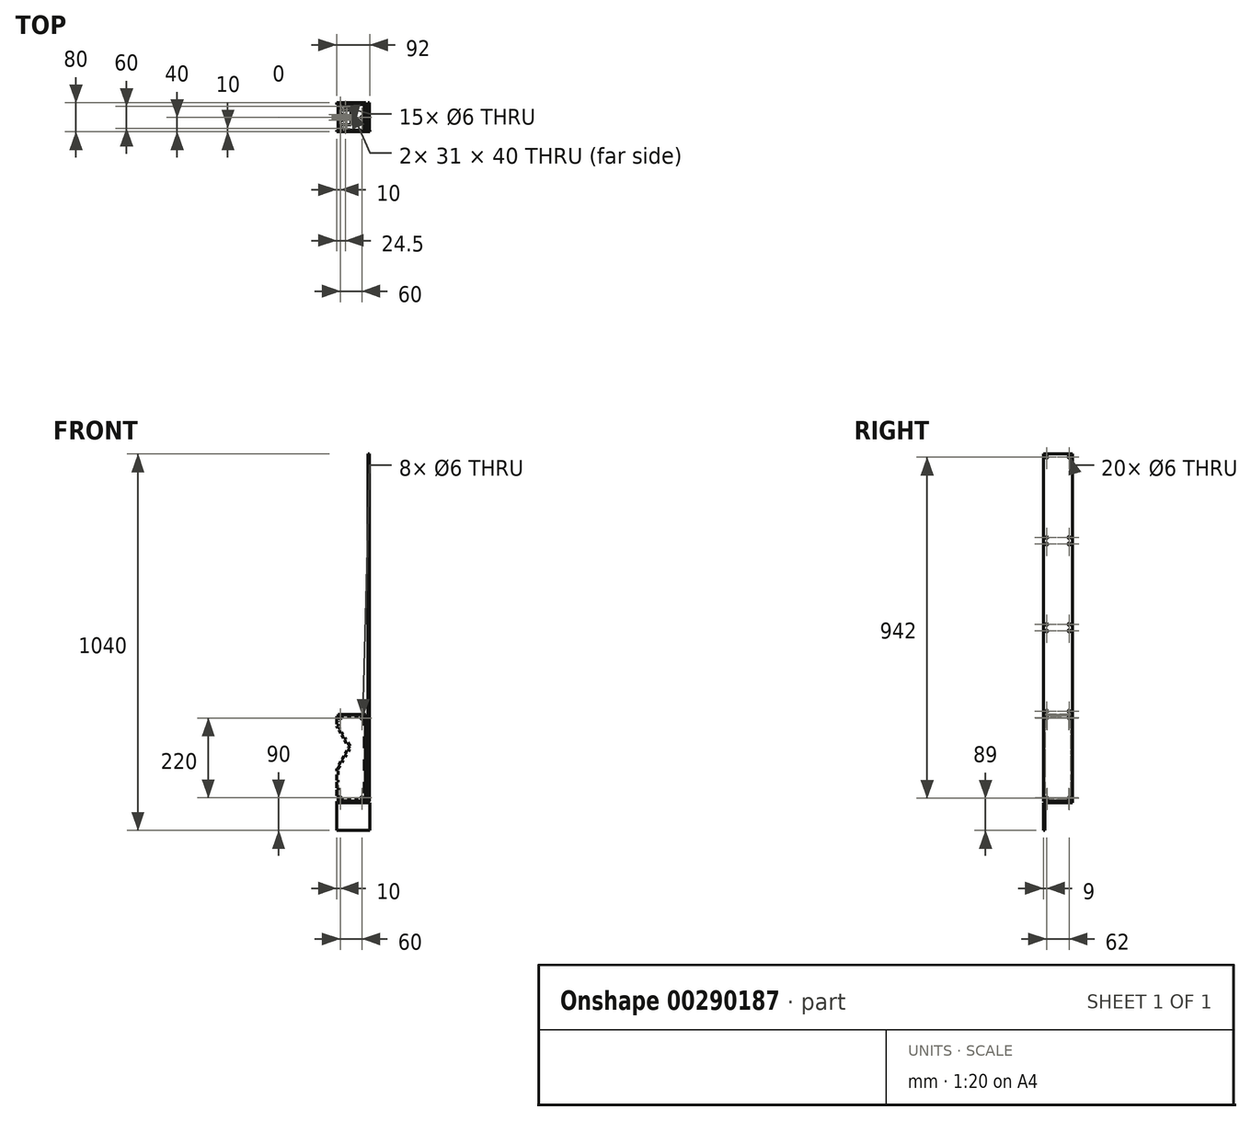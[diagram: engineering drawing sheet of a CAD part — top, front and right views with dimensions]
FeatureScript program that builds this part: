
annotation { "Feature Type Name" : "Feature", "Feature Type Description" : "" }
export const myFeature = defineFeature(function(context is Context, id is Id, definition is map)
    precondition{}
    {
        {
            assignVariable(context, id + "F0", {"name" : "WT", "anyValue" : 4});
        }
        {
            assignVariable(context, id + "F1", {"name" : "HD", "anyValue" : 3});
        }
        {
            var Q0;
            Q0=qCreatedBy(makeId("Front.planeOp"),FACE);
            var sketch = newSketch(context, id + "F2", { "sketchPlane" : qUnion([Q0])});
            skLineSegment(sketch, "E0", {"start": v(0, 0) * mm, "end": v(0, 240) * mm});
            skLineSegment(sketch, "E1", {"start": v(0, 120) * mm, "end": v(-80, 120) * mm, "construction": true});
            skLineSegment(sketch, "E2", {"start": v(0, 0) * mm, "end": v(-80, 0) * mm});
            skLineSegment(sketch, "E3", {"start": v(-80, 0) * mm, "end": v(-80, 90.56) * mm});
            skLineSegment(sketch, "E4", {"start": v(-80, 90.56) * mm, "end": v(-46, 149.44) * mm});
            skLineSegment(sketch, "E5", {"start": v(-46, 149.44) * mm, "end": v(-80, 208.33) * mm});
            skLineSegment(sketch, "E6", {"start": v(-80, 208.33) * mm, "end": v(-80, 240) * mm});
            skLineSegment(sketch, "E7", {"start": v(-80, 240) * mm, "end": v(0, 240) * mm});
            skLineSegment(sketch, "E8", {"start": v(-80, 90.56) * mm, "end": v(0, 90.56) * mm, "construction": true});
            skLineSegment(sketch, "E9", {"start": v(-80, 208.33) * mm, "end": v(0, 208.33) * mm, "construction": true});
            skPoint(sketch, "E10", {"position": v(-63, 120) * mm});
            skLineSegment(sketch, "E11", {"start": v(-80, 90.56) * mm, "end": v(-76, 90.56) * mm});
            skLineSegment(sketch, "E12", {"start": v(-76, 90.56) * mm, "end": v(-76, 0) * mm});
            skLineSegment(sketch, "E13", {"start": v(-4, 0) * mm, "end": v(-4, 240) * mm});
            skLineSegment(sketch, "E14", {"start": v(0, 236) * mm, "end": v(-80, 236) * mm});
            skLineSegment(sketch, "E15", {"start": v(-76, 240) * mm, "end": v(-76, 208.33) * mm});
            skLineSegment(sketch, "E16", {"start": v(-80, 208.33) * mm, "end": v(-76, 208.33) * mm});
            skLineSegment(sketch, "E17", {"start": v(-80, 4) * mm, "end": v(0, 4) * mm});
            skLineSegment(sketch, "E18", {"start": v(-80, 90.56) * mm, "end": v(-76.54, 88.56) * mm});
            skLineSegment(sketch, "E19", {"start": v(-76.54, 88.56) * mm, "end": v(-42.54, 147.44) * mm});
            skLineSegment(sketch, "E20", {"start": v(-80, 208.33) * mm, "end": v(-76.54, 210.33) * mm});
            skLineSegment(sketch, "E21", {"start": v(-76.54, 210.33) * mm, "end": v(-41.38, 149.44) * mm});
            skLineSegment(sketch, "E22", {"start": v(-46, 149.44) * mm, "end": v(-44.85, 147.44) * mm});
            skLineSegment(sketch, "E23", {"start": v(-44.85, 147.44) * mm, "end": v(-41.38, 149.44) * mm});
            skLineSegment(sketch, "E24", {"start": v(-42.54, 147.44) * mm, "end": v(-41.38, 149.44) * mm});
            skLineSegment(sketch, "E25", {"start": v(-46, 149.44) * mm, "end": v(-44.85, 151.44) * mm});
            skLineSegment(sketch, "E26", {"start": v(-44.85, 151.44) * mm, "end": v(-41.38, 149.44) * mm});
            skLineSegment(sketch, "E27", {"start": v(-75.54, 208.6) * mm, "end": v(-79, 206.6) * mm});
            skLineSegment(sketch, "E28", {"start": v(-46.58, 150.44) * mm, "end": v(-43.11, 152.44) * mm});
            skPoint(sketch, "E29", {"position": v(-79, 206.6) * mm});
            skPoint(sketch, "E30", {"position": v(-46.58, 150.44) * mm});
            skPoint(sketch, "E31", {"position": v(-80, 88.56) * mm});
            skCircle(sketch, "E32", {"center": v(-70, 230) * mm, "radius": 3 * mm});
            skLineSegment(sketch, "E33", {"start": v(-40, 208.33) * mm, "end": v(-40, 225.54) * mm, "construction": true});
            skCircle(sketch, "E34.MirrorC", {"center": v(-10, 230) * mm, "radius": 3 * mm});
            skCircle(sketch, "E35.MirrorC", {"center": v(-70, 10) * mm, "radius": 3 * mm});
            skCircle(sketch, "E36.MirrorC", {"center": v(-10, 10) * mm, "radius": 3 * mm});
            skSolve(sketch);
        }
        {
            var Q0;
            Q0=qCreatedBy(makeId("Front.planeOp"),FACE);
            var sketch = newSketch(context, id + "F3", { "sketchPlane" : qUnion([Q0])});
            skLineSegment(sketch, "E37.0", {"start": v(-80, 240) * mm, "end": v(0, 240) * mm});
            skLineSegment(sketch, "E37.1", {"start": v(-80, 208.33) * mm, "end": v(-80, 240) * mm});
            skLineSegment(sketch, "E37.2", {"start": v(-46, 149.44) * mm, "end": v(-80, 208.33) * mm});
            skLineSegment(sketch, "E37.3", {"start": v(-80, 90.56) * mm, "end": v(-46, 149.44) * mm});
            skLineSegment(sketch, "E37.4", {"start": v(-80, 0) * mm, "end": v(-80, 90.56) * mm});
            skLineSegment(sketch, "E37.5", {"start": v(0, 0) * mm, "end": v(-80, 0) * mm});
            skLineSegment(sketch, "E37.6", {"start": v(0, 0) * mm, "end": v(0, 240) * mm});
            skCircle(sketch, "E38.0", {"center": v(-70, 230) * mm, "radius": 3 * mm});
            skCircle(sketch, "E38.1", {"center": v(-10, 230) * mm, "radius": 3 * mm});
            skCircle(sketch, "E38.2", {"center": v(-70, 10) * mm, "radius": 3 * mm});
            skCircle(sketch, "E38.3", {"center": v(-10, 10) * mm, "radius": 3 * mm});
            skLineSegment(sketch, "E39", {"start": v(0, -80) * mm, "end": v(-80, -80) * mm});
            skLineSegment(sketch, "E40", {"start": v(-80, -80) * mm, "end": v(-80, 0) * mm});
            skLineSegment(sketch, "E41", {"start": v(0, 0) * mm, "end": v(12, 0) * mm});
            skLineSegment(sketch, "E42", {"start": v(12, 0) * mm, "end": v(12, -80) * mm});
            skLineSegment(sketch, "E43", {"start": v(12, -80) * mm, "end": v(0, -80) * mm});
            skSolve(sketch);
        }
        {
            var Q0;
            Q0=sQuery(id+"F2.wireOp",EDGE,"E7");
            cPlane(context, id + "F4", {"entities" : qUnion([Q0]), "cplaneType" : CPlaneType.LINE_ANGLE, "offset" : 25 * mm, "angle" : 90 * degree, "width" : 150 * mm, "height" : 150 * mm});
        }
        {
            var Q0;
            Q0=qCreatedBy(id+"F4.planeOp",FACE);
            var sketch = newSketch(context, id + "F5", { "sketchPlane" : qUnion([Q0])});
            skLineSegment(sketch, "E44.0", {"start": v(-80, 0) * mm, "end": v(0, 0) * mm});
            skLineSegment(sketch, "E45", {"start": v(-80, 0) * mm, "end": v(-80, 80) * mm});
            skLineSegment(sketch, "E46", {"start": v(-80, 80) * mm, "end": v(0, 80) * mm});
            skLineSegment(sketch, "E47", {"start": v(0, 80) * mm, "end": v(0, 0) * mm});
            skLineSegment(sketch, "E48", {"start": v(0, 40) * mm, "end": v(-80, 40) * mm, "construction": true});
            skLineSegment(sketch, "E49", {"start": v(-80, 76) * mm, "end": v(0, 76) * mm});
            skLineSegment(sketch, "E50", {"start": v(-70, 80) * mm, "end": v(-70, 76) * mm});
            skLineSegment(sketch, "E51.1.0.0", {"start": v(-60, 80) * mm, "end": v(-60, 76) * mm});
            skLineSegment(sketch, "E51.2.0.0", {"start": v(-50, 80) * mm, "end": v(-50, 76) * mm});
            skLineSegment(sketch, "E51.3.0.0", {"start": v(-40, 80) * mm, "end": v(-40, 76) * mm});
            skLineSegment(sketch, "E51.4.0.0", {"start": v(-30, 80) * mm, "end": v(-30, 76) * mm});
            skLineSegment(sketch, "E51.5.0.0", {"start": v(-20, 80) * mm, "end": v(-20, 76) * mm});
            skLineSegment(sketch, "E51.6.0.0", {"start": v(-10, 80) * mm, "end": v(-10, 76) * mm});
            skLineSegment(sketch, "E51.direction1", {"start": v(-70, 76) * mm, "end": v(-60, 76) * mm, "construction": true});
            skLineSegment(sketch, "E52.MirrorCS", {"start": v(-80, 4) * mm, "end": v(0, 4) * mm});
            skLineSegment(sketch, "E53.MirrorCS", {"start": v(-70, 0) * mm, "end": v(-70, 4) * mm});
            skLineSegment(sketch, "E54.MirrorCS", {"start": v(-60, 0) * mm, "end": v(-60, 4) * mm});
            skLineSegment(sketch, "E55.MirrorCS", {"start": v(-50, 0) * mm, "end": v(-50, 4) * mm});
            skLineSegment(sketch, "E56.MirrorCS", {"start": v(-40, 0) * mm, "end": v(-40, 4) * mm});
            skLineSegment(sketch, "E57.MirrorCS", {"start": v(-30, 0) * mm, "end": v(-30, 4) * mm});
            skLineSegment(sketch, "E58.MirrorCS", {"start": v(-20, 0) * mm, "end": v(-20, 4) * mm});
            skLineSegment(sketch, "E59.MirrorCS", {"start": v(-10, 0) * mm, "end": v(-10, 4) * mm});
            skLineSegment(sketch, "E60", {"start": v(-76, 80) * mm, "end": v(-76, 0) * mm});
            skLineSegment(sketch, "E61", {"start": v(-80, 71.1) * mm, "end": v(-76, 71.1) * mm});
            skLineSegment(sketch, "E62.0.1.0", {"start": v(-80, 62.34) * mm, "end": v(-76, 62.34) * mm});
            skLineSegment(sketch, "E62.0.2.0", {"start": v(-80, 53.6) * mm, "end": v(-76, 53.6) * mm});
            skLineSegment(sketch, "E62.0.3.0", {"start": v(-80, 44.84) * mm, "end": v(-76, 44.84) * mm});
            skLineSegment(sketch, "E62.0.4.0", {"start": v(-80, 36.1) * mm, "end": v(-76, 36.1) * mm});
            skLineSegment(sketch, "E62.0.5.0", {"start": v(-80, 27.34) * mm, "end": v(-76, 27.34) * mm});
            skLineSegment(sketch, "E62.0.6.0", {"start": v(-80, 18.6) * mm, "end": v(-76, 18.6) * mm});
            skLineSegment(sketch, "E62.direction1", {"start": v(-86.03, 71.1) * mm, "end": v(-80, 71.1) * mm, "construction": true});
            skLineSegment(sketch, "E62.direction2", {"start": v(-80, 71.1) * mm, "end": v(-80, 62.34) * mm, "construction": true});
            skLineSegment(sketch, "E63", {"start": v(-40, 40) * mm, "end": v(-40, 50.28) * mm, "construction": true});
            skLineSegment(sketch, "E64.MirrorCS", {"start": v(0, 18.6) * mm, "end": v(-4, 18.6) * mm});
            skLineSegment(sketch, "E65.MirrorCS", {"start": v(0, 27.34) * mm, "end": v(-4, 27.34) * mm});
            skLineSegment(sketch, "E66.MirrorCS", {"start": v(0, 36.1) * mm, "end": v(-4, 36.1) * mm});
            skLineSegment(sketch, "E67.MirrorCS", {"start": v(0, 44.84) * mm, "end": v(-4, 44.84) * mm});
            skLineSegment(sketch, "E68.MirrorCS", {"start": v(0, 53.6) * mm, "end": v(-4, 53.6) * mm});
            skLineSegment(sketch, "E69.MirrorCS", {"start": v(0, 62.34) * mm, "end": v(-4, 62.34) * mm});
            skLineSegment(sketch, "E70.MirrorCS", {"start": v(0, 71.1) * mm, "end": v(-4, 71.1) * mm});
            skLineSegment(sketch, "E71.MirrorCS", {"start": v(-4, 80) * mm, "end": v(-4, 0) * mm});
            skLineSegment(sketch, "E72.bottom", {"start": v(-40, 20) * mm, "end": v(-71, 20) * mm});
            skLineSegment(sketch, "E72.top", {"start": v(-40, 60) * mm, "end": v(-71, 60) * mm});
            skLineSegment(sketch, "E72.left", {"start": v(-9, 40) * mm, "end": v(-9, 60) * mm, "construction": true});
            skLineSegment(sketch, "E72.right", {"start": v(-71, 20) * mm, "end": v(-71, 60) * mm});
            skPoint(sketch, "E72.middle", {"position": v(-40, 40) * mm});
            skCircle(sketch, "E73", {"center": v(-10, 40) * mm, "radius": 3 * mm});
            skCircle(sketch, "E74.MirrorC", {"center": v(-70, 70) * mm, "radius": 3 * mm});
            skLineSegment(sketch, "E75", {"start": v(-40, 20) * mm, "end": v(-40, 60) * mm});
            skPoint(sketch, "E76.orphan", {"position": v(-9, 20) * mm});
            skCircle(sketch, "E77.MirrorC", {"center": v(-70, 10) * mm, "radius": 3 * mm});
            skLineSegment(sketch, "E78.0.0.7", {"start": v(-80, 9.84) * mm, "end": v(-76, 9.84) * mm});
            skLineSegment(sketch, "E79.MirrorCS", {"start": v(0, 9.84) * mm, "end": v(-4, 9.84) * mm});
            skSolve(sketch);
        }
        {
            var Q0;
            Q0=sQuery(id+"F2.wireOp",EDGE,"E0");
            cPlane(context, id + "F6", {"entities" : qUnion([Q0]), "cplaneType" : CPlaneType.LINE_ANGLE, "offset" : 25 * mm, "angle" : 0 * degree, "width" : 150 * mm, "height" : 150 * mm});
        }
        {
            var Q0;
            Q0=qCreatedBy(id+"F6.planeOp",FACE);
            var sketch = newSketch(context, id + "F7", { "sketchPlane" : qUnion([Q0])});
            skLineSegment(sketch, "E80.0", {"start": v(0, 0) * mm, "end": v(0, 240) * mm});
            skLineSegment(sketch, "E81.0", {"start": v(80, 240) * mm, "end": v(0, 240) * mm});
            skLineSegment(sketch, "E82", {"start": v(80, 240) * mm, "end": v(80, 0) * mm});
            skLineSegment(sketch, "E83", {"start": v(80, 0) * mm, "end": v(0, 0) * mm});
            skLineSegment(sketch, "E84", {"start": v(4, 240) * mm, "end": v(4, 0) * mm});
            skLineSegment(sketch, "E85", {"start": v(0, 210) * mm, "end": v(4, 210) * mm});
            skLineSegment(sketch, "E86.0.1.0", {"start": v(0, 178.75) * mm, "end": v(4, 178.75) * mm});
            skLineSegment(sketch, "E86.0.2.0", {"start": v(0, 147.5) * mm, "end": v(4, 147.5) * mm});
            skLineSegment(sketch, "E86.0.3.0", {"start": v(0, 116.25) * mm, "end": v(4, 116.25) * mm});
            skLineSegment(sketch, "E86.0.4.0", {"start": v(0, 85) * mm, "end": v(4, 85) * mm});
            skLineSegment(sketch, "E86.0.5.0", {"start": v(0, 53.75) * mm, "end": v(4, 53.75) * mm});
            skLineSegment(sketch, "E86.0.6.0", {"start": v(0, 22.5) * mm, "end": v(4, 22.5) * mm});
            skLineSegment(sketch, "E86.direction1", {"start": v(-5.68, 210) * mm, "end": v(0, 210) * mm, "construction": true});
            skLineSegment(sketch, "E86.direction2", {"start": v(0, 210) * mm, "end": v(0, 178.75) * mm, "construction": true});
            skLineSegment(sketch, "E87", {"start": v(40, 240) * mm, "end": v(40, 220.49) * mm, "construction": true});
            skPoint(sketch, "E87.endSnap0", {"position": v(40, 240) * mm});
            skLineSegment(sketch, "E88.MirrorCS", {"start": v(76, 240) * mm, "end": v(76, 0) * mm});
            skLineSegment(sketch, "E89.MirrorCS", {"start": v(80, 210) * mm, "end": v(76, 210) * mm});
            skLineSegment(sketch, "E90.MirrorCS", {"start": v(80, 178.75) * mm, "end": v(76, 178.75) * mm});
            skLineSegment(sketch, "E91.MirrorCS", {"start": v(80, 147.5) * mm, "end": v(76, 147.5) * mm});
            skLineSegment(sketch, "E92.MirrorCS", {"start": v(80, 116.25) * mm, "end": v(76, 116.25) * mm});
            skLineSegment(sketch, "E93.MirrorCS", {"start": v(80, 85) * mm, "end": v(76, 85) * mm});
            skLineSegment(sketch, "E94.MirrorCS", {"start": v(80, 53.75) * mm, "end": v(76, 53.75) * mm});
            skLineSegment(sketch, "E95.MirrorCS", {"start": v(80, 22.5) * mm, "end": v(76, 22.5) * mm});
            skCircle(sketch, "E96", {"center": v(10, 230) * mm, "radius": 3 * mm});
            skCircle(sketch, "E97.MirrorC", {"center": v(70, 230) * mm, "radius": 3 * mm});
            skLineSegment(sketch, "E98", {"start": v(76, 120) * mm, "end": v(4, 120) * mm, "construction": true});
            skCircle(sketch, "E99.MirrorC", {"center": v(10, 10) * mm, "radius": 3 * mm});
            skCircle(sketch, "E100.MirrorC", {"center": v(70, 10) * mm, "radius": 3 * mm});
            skSolve(sketch);
        }
        {
            var Q0;
            Q0=sQuery(id+"F2.wireOp",EDGE,"E2");
            cPlane(context, id + "F8", {"entities" : qUnion([Q0]), "cplaneType" : CPlaneType.LINE_ANGLE, "offset" : 25 * mm, "angle" : 90 * degree, "width" : 150 * mm, "height" : 150 * mm});
        }
        {
            var Q0;
            Q0=qCreatedBy(id+"F8.planeOp",FACE);
            var sketch = newSketch(context, id + "F9", { "sketchPlane" : qUnion([Q0])});
            skLineSegment(sketch, "E101.0", {"start": v(-80, 0) * mm, "end": v(0, 0) * mm});
            skLineSegment(sketch, "E101.1", {"start": v(0, 80) * mm, "end": v(0, 0) * mm});
            skLineSegment(sketch, "E101.2", {"start": v(-80, 0) * mm, "end": v(-80, 80) * mm});
            skLineSegment(sketch, "E101.3", {"start": v(-80, 80) * mm, "end": v(0, 80) * mm});
            skLineSegment(sketch, "E101.4", {"start": v(-80, 76) * mm, "end": v(0, 76) * mm});
            skLineSegment(sketch, "E101.5", {"start": v(-4, 80) * mm, "end": v(-4, 0) * mm});
            skLineSegment(sketch, "E101.6", {"start": v(-76, 80) * mm, "end": v(-76, 0) * mm});
            skLineSegment(sketch, "E101.7", {"start": v(-70, 80) * mm, "end": v(-70, 76) * mm});
            skLineSegment(sketch, "E101.8", {"start": v(-60, 80) * mm, "end": v(-60, 76) * mm});
            skLineSegment(sketch, "E101.9", {"start": v(-50, 80) * mm, "end": v(-50, 76) * mm});
            skLineSegment(sketch, "E101.10", {"start": v(-40, 80) * mm, "end": v(-40, 76) * mm});
            skLineSegment(sketch, "E101.11", {"start": v(-30, 80) * mm, "end": v(-30, 76) * mm});
            skLineSegment(sketch, "E101.12", {"start": v(-20, 80) * mm, "end": v(-20, 76) * mm});
            skLineSegment(sketch, "E101.13", {"start": v(-10, 80) * mm, "end": v(-10, 76) * mm});
            skLineSegment(sketch, "E101.14", {"start": v(0, 71.1) * mm, "end": v(-4, 71.1) * mm});
            skLineSegment(sketch, "E101.15", {"start": v(0, 62.34) * mm, "end": v(-4, 62.34) * mm});
            skLineSegment(sketch, "E101.16", {"start": v(0, 53.6) * mm, "end": v(-4, 53.6) * mm});
            skLineSegment(sketch, "E101.17", {"start": v(0, 36.1) * mm, "end": v(-4, 36.1) * mm});
            skLineSegment(sketch, "E101.18", {"start": v(0, 27.34) * mm, "end": v(-4, 27.34) * mm});
            skLineSegment(sketch, "E101.19", {"start": v(0, 18.6) * mm, "end": v(-4, 18.6) * mm});
            skLineSegment(sketch, "E101.20", {"start": v(-80, 4) * mm, "end": v(0, 4) * mm});
            skLineSegment(sketch, "E101.21", {"start": v(-10, 0) * mm, "end": v(-10, 4) * mm});
            skLineSegment(sketch, "E101.22", {"start": v(-20, 0) * mm, "end": v(-20, 4) * mm});
            skLineSegment(sketch, "E101.23", {"start": v(-30, 0) * mm, "end": v(-30, 4) * mm});
            skLineSegment(sketch, "E101.24", {"start": v(-40, 0) * mm, "end": v(-40, 4) * mm});
            skLineSegment(sketch, "E101.25", {"start": v(-50, 0) * mm, "end": v(-50, 4) * mm});
            skLineSegment(sketch, "E101.26", {"start": v(-60, 0) * mm, "end": v(-60, 4) * mm});
            skLineSegment(sketch, "E101.27", {"start": v(-70, 0) * mm, "end": v(-70, 4) * mm});
            skLineSegment(sketch, "E101.28", {"start": v(-80, 18.6) * mm, "end": v(-76, 18.6) * mm});
            skLineSegment(sketch, "E101.29", {"start": v(-80, 27.34) * mm, "end": v(-76, 27.34) * mm});
            skLineSegment(sketch, "E101.30", {"start": v(-80, 36.1) * mm, "end": v(-76, 36.1) * mm});
            skLineSegment(sketch, "E101.31", {"start": v(-80, 44.84) * mm, "end": v(-76, 44.84) * mm});
            skLineSegment(sketch, "E101.32", {"start": v(-80, 53.6) * mm, "end": v(-76, 53.6) * mm});
            skLineSegment(sketch, "E101.33", {"start": v(-80, 62.34) * mm, "end": v(-76, 62.34) * mm});
            skLineSegment(sketch, "E101.34", {"start": v(-80, 71.1) * mm, "end": v(-76, 71.1) * mm});
            skLineSegment(sketch, "E101.35", {"start": v(0, 44.84) * mm, "end": v(-4, 44.84) * mm});
            skCircle(sketch, "E102.0", {"center": v(-70, 70) * mm, "radius": 3 * mm});
            skCircle(sketch, "E102.2", {"center": v(-10, 40) * mm, "radius": 3 * mm});
            skLineSegment(sketch, "E103.0", {"start": v(-9, 40) * mm, "end": v(-9, 60) * mm});
            skLineSegment(sketch, "E104", {"start": v(-9, 50) * mm, "end": v(-37.11, 50) * mm, "construction": true});
            skLineSegment(sketch, "E105.0", {"start": v(-71, 20) * mm, "end": v(-71, 60) * mm});
            skLineSegment(sketch, "E106", {"start": v(-71, 40) * mm, "end": v(-47.56, 40) * mm, "construction": true});
            skPoint(sketch, "E106.endSnap0", {"position": v(-71, 40) * mm});
            skCircle(sketch, "E107", {"center": v(-68, 40) * mm, "radius": 3 * mm});
            skLineSegment(sketch, "E108", {"start": v(-68, 40) * mm, "end": v(-68, 48) * mm, "construction": true});
            skCircle(sketch, "E109", {"center": v(-68, 48) * mm, "radius": 3 * mm});
            skCircle(sketch, "E110.MirrorC", {"center": v(-68, 32) * mm, "radius": 3 * mm});
            skLineSegment(sketch, "E111", {"start": v(-68, 44) * mm, "end": v(-60, 44) * mm, "construction": true});
            skCircle(sketch, "E112", {"center": v(-60, 44) * mm, "radius": 3 * mm});
            skCircle(sketch, "E113.MirrorC", {"center": v(-60, 36) * mm, "radius": 3 * mm});
            skLineSegment(sketch, "E114", {"start": v(-60, 44) * mm, "end": v(-60, 31.93) * mm, "construction": true});
            skCircle(sketch, "E115.MirrorC", {"center": v(-52, 40) * mm, "radius": 3 * mm});
            skCircle(sketch, "E116.0", {"center": v(-70, 10) * mm, "radius": 3 * mm});
            skSolve(sketch);
        }
        {
            var Q0;
            Q0=sQuery(id+"F7.wireOp",EDGE,"E82");
            cPlane(context, id + "F10", {"entities" : qUnion([Q0]), "cplaneType" : CPlaneType.LINE_ANGLE, "offset" : 25 * mm, "angle" : 90 * degree, "width" : 150 * mm, "height" : 150 * mm});
        }
        {
            var Q0;
            Q0=qCreatedBy(id+"F10.planeOp",FACE);
            var sketch = newSketch(context, id + "F11", { "sketchPlane" : qUnion([Q0])});
            skLineSegment(sketch, "E117.0", {"start": v(80, 208.33) * mm, "end": v(80, 240) * mm});
            skLineSegment(sketch, "E117.1", {"start": v(46, 149.44) * mm, "end": v(80, 208.33) * mm});
            skLineSegment(sketch, "E117.2", {"start": v(80, 90.56) * mm, "end": v(46, 149.44) * mm});
            skLineSegment(sketch, "E117.3", {"start": v(80, 0) * mm, "end": v(80, 90.56) * mm});
            skLineSegment(sketch, "E117.4", {"start": v(0, 0) * mm, "end": v(80, 0) * mm});
            skLineSegment(sketch, "E117.5", {"start": v(0, 0) * mm, "end": v(0, 240) * mm});
            skLineSegment(sketch, "E117.6", {"start": v(80, 240) * mm, "end": v(0, 240) * mm});
            skCircle(sketch, "E118", {"center": v(10, 230) * mm, "radius": 3 * mm});
            skLineSegment(sketch, "E119", {"start": v(40, 240) * mm, "end": v(40, 223.94) * mm, "construction": true});
            skCircle(sketch, "E120.MirrorC", {"center": v(70, 230) * mm, "radius": 3 * mm});
            skCircle(sketch, "E121.MirrorC", {"center": v(10, 10) * mm, "radius": 3 * mm});
            skCircle(sketch, "E122.MirrorC", {"center": v(70, 10) * mm, "radius": 3 * mm});
            skSolve(sketch);
        }
        {
            var Q0;
            Q0=sQuery(id+"F2.wireOp",EDGE,"E6");
            cPlane(context, id + "F12", {"entities" : qUnion([Q0]), "cplaneType" : CPlaneType.LINE_ANGLE, "offset" : 25 * mm, "angle" : 0 * degree, "width" : 150 * mm, "height" : 150 * mm});
        }
        {
            var Q0;
            Q0=qCreatedBy(id+"F12.planeOp",FACE);
            var sketch = newSketch(context, id + "F13", { "sketchPlane" : qUnion([Q0])});
            skLineSegment(sketch, "E123.0", {"start": v(0, 208.33) * mm, "end": v(0, 240) * mm});
            skLineSegment(sketch, "E124.0", {"start": v(0, 240) * mm, "end": v(80, 240) * mm});
            skLineSegment(sketch, "E125", {"start": v(80, 240) * mm, "end": v(80, 208.33) * mm});
            skLineSegment(sketch, "E126", {"start": v(80, 208.33) * mm, "end": v(0, 208.33) * mm});
            skLineSegment(sketch, "E127", {"start": v(80, 224.17) * mm, "end": v(0, 224.17) * mm, "construction": true});
            skLineSegment(sketch, "E128", {"start": v(80, 227.37) * mm, "end": v(76, 227.37) * mm});
            skLineSegment(sketch, "E129", {"start": v(76, 227.37) * mm, "end": v(76, 224.17) * mm});
            skLineSegment(sketch, "E130.MirrorCS", {"start": v(76, 220.97) * mm, "end": v(76, 224.17) * mm});
            skLineSegment(sketch, "E131.MirrorCS", {"start": v(80, 220.97) * mm, "end": v(76, 220.97) * mm});
            skLineSegment(sketch, "E132", {"start": v(80, 240) * mm, "end": v(0, 224.17) * mm, "construction": true});
            skLineSegment(sketch, "E133", {"start": v(40, 232.08) * mm, "end": v(80, 232.08) * mm, "construction": true});
            skLineSegment(sketch, "E134", {"start": v(80, 235.28) * mm, "end": v(76, 235.28) * mm});
            skLineSegment(sketch, "E135", {"start": v(76, 235.28) * mm, "end": v(76, 232.08) * mm});
            skLineSegment(sketch, "E136.MirrorCS", {"start": v(76, 228.88) * mm, "end": v(76, 232.08) * mm});
            skLineSegment(sketch, "E137.MirrorCS", {"start": v(80, 228.88) * mm, "end": v(76, 228.88) * mm});
            skLineSegment(sketch, "E138.MirrorCS", {"start": v(80, 219.45) * mm, "end": v(76, 219.45) * mm});
            skLineSegment(sketch, "E139.MirrorCS", {"start": v(76, 219.45) * mm, "end": v(76, 216.25) * mm});
            skLineSegment(sketch, "E140.MirrorCS", {"start": v(76, 213.05) * mm, "end": v(76, 216.25) * mm});
            skLineSegment(sketch, "E141.MirrorCS", {"start": v(80, 213.05) * mm, "end": v(76, 213.05) * mm});
            skLineSegment(sketch, "E142", {"start": v(40, 224.17) * mm, "end": v(40, 240) * mm, "construction": true});
            skLineSegment(sketch, "E143.MirrorCS", {"start": v(0, 235.28) * mm, "end": v(4, 235.28) * mm});
            skLineSegment(sketch, "E144.MirrorCS", {"start": v(4, 235.28) * mm, "end": v(4, 232.08) * mm});
            skLineSegment(sketch, "E145.MirrorCS", {"start": v(4, 228.88) * mm, "end": v(4, 232.08) * mm});
            skLineSegment(sketch, "E146.MirrorCS", {"start": v(0, 228.88) * mm, "end": v(4, 228.88) * mm});
            skLineSegment(sketch, "E147.MirrorCS", {"start": v(0, 227.37) * mm, "end": v(4, 227.37) * mm});
            skLineSegment(sketch, "E148.MirrorCS", {"start": v(4, 227.37) * mm, "end": v(4, 224.17) * mm});
            skLineSegment(sketch, "E149.MirrorCS", {"start": v(4, 220.97) * mm, "end": v(4, 224.17) * mm});
            skLineSegment(sketch, "E150.MirrorCS", {"start": v(0, 220.97) * mm, "end": v(4, 220.97) * mm});
            skLineSegment(sketch, "E151.MirrorCS", {"start": v(0, 219.45) * mm, "end": v(4, 219.45) * mm});
            skLineSegment(sketch, "E152.MirrorCS", {"start": v(4, 219.45) * mm, "end": v(4, 216.25) * mm});
            skLineSegment(sketch, "E153.MirrorCS", {"start": v(4, 213.05) * mm, "end": v(4, 216.25) * mm});
            skLineSegment(sketch, "E154.MirrorCS", {"start": v(0, 213.05) * mm, "end": v(4, 213.05) * mm});
            skSolve(sketch);
        }
        {
            var Q0;
            Q0=sQuery(id+"F11.wireOp",EDGE,"E117.3");
            cPlane(context, id + "F14", {"entities" : qUnion([Q0]), "cplaneType" : CPlaneType.LINE_ANGLE, "offset" : 25 * mm, "angle" : 0 * degree, "width" : 150 * mm, "height" : 150 * mm});
        }
        {
            var Q0;
            Q0=qCreatedBy(id+"F14.planeOp",FACE);
            var sketch = newSketch(context, id + "F15", { "sketchPlane" : qUnion([Q0])});
            skLineSegment(sketch, "E155.0", {"start": v(80, 0) * mm, "end": v(80, 90.56) * mm});
            skLineSegment(sketch, "E156.0", {"start": v(0, 0) * mm, "end": v(80, 0) * mm});
            skLineSegment(sketch, "E157", {"start": v(80, 88.56) * mm, "end": v(0, 88.56) * mm});
            skLineSegment(sketch, "E158", {"start": v(0, 88.56) * mm, "end": v(0, 0) * mm});
            skLineSegment(sketch, "E159", {"start": v(80, 45.28) * mm, "end": v(0, 44.28) * mm, "construction": true});
            skLineSegment(sketch, "E160", {"start": v(0, 44.28) * mm, "end": v(80, 88.56) * mm, "construction": true});
            skLineSegment(sketch, "E161", {"start": v(80, 53.28) * mm, "end": v(76, 53.23) * mm});
            skLineSegment(sketch, "E162", {"start": v(76, 53.23) * mm, "end": v(76, 45.23) * mm});
            skLineSegment(sketch, "E163.MirrorCS", {"start": v(76.2, 37.23) * mm, "end": v(76, 45.23) * mm});
            skLineSegment(sketch, "E164.MirrorCS", {"start": v(80.2, 37.28) * mm, "end": v(76.2, 37.23) * mm});
            skLineSegment(sketch, "E165", {"start": v(40, 66.42) * mm, "end": v(80, 66.42) * mm, "construction": true});
            skLineSegment(sketch, "E166", {"start": v(80, 74.42) * mm, "end": v(76, 74.42) * mm});
            skLineSegment(sketch, "E167", {"start": v(76, 74.42) * mm, "end": v(76, 66.42) * mm});
            skLineSegment(sketch, "E168.MirrorCS", {"start": v(76, 58.42) * mm, "end": v(76, 66.42) * mm});
            skLineSegment(sketch, "E169.MirrorCS", {"start": v(80, 58.42) * mm, "end": v(76, 58.42) * mm});
            skLineSegment(sketch, "E170.MirrorCS", {"start": v(80.33, 32.14) * mm, "end": v(76.33, 32.04) * mm});
            skLineSegment(sketch, "E171.MirrorCS", {"start": v(76.33, 32.04) * mm, "end": v(76.53, 24.05) * mm});
            skLineSegment(sketch, "E172.MirrorCS", {"start": v(76.73, 16.05) * mm, "end": v(76.53, 24.05) * mm});
            skLineSegment(sketch, "E173.MirrorCS", {"start": v(80.73, 16.15) * mm, "end": v(76.73, 16.05) * mm});
            skLineSegment(sketch, "E174", {"start": v(40, 66.42) * mm, "end": v(40, 35.3) * mm, "construction": true});
            skPoint(sketch, "E174.endSnap0", {"position": v(40, 44.78) * mm});
            skLineSegment(sketch, "E175.MirrorCS", {"start": v(0, 74.42) * mm, "end": v(4, 74.42) * mm});
            skLineSegment(sketch, "E176.MirrorCS", {"start": v(4, 74.42) * mm, "end": v(4, 66.42) * mm});
            skLineSegment(sketch, "E177.MirrorCS", {"start": v(4, 58.42) * mm, "end": v(4, 66.42) * mm});
            skLineSegment(sketch, "E178.MirrorCS", {"start": v(0, 58.42) * mm, "end": v(4, 58.42) * mm});
            skLineSegment(sketch, "E179.MirrorCS", {"start": v(0, 53.28) * mm, "end": v(4, 53.23) * mm});
            skLineSegment(sketch, "E180.MirrorCS", {"start": v(4, 53.23) * mm, "end": v(4, 45.23) * mm});
            skLineSegment(sketch, "E181.MirrorCS", {"start": v(3.8, 37.23) * mm, "end": v(4, 45.23) * mm});
            skLineSegment(sketch, "E182.MirrorCS", {"start": v(-0.2, 37.28) * mm, "end": v(3.8, 37.23) * mm});
            skLineSegment(sketch, "E183.MirrorCS", {"start": v(-0.33, 32.14) * mm, "end": v(3.67, 32.04) * mm});
            skLineSegment(sketch, "E184.MirrorCS", {"start": v(3.67, 32.04) * mm, "end": v(3.47, 24.05) * mm});
            skLineSegment(sketch, "E185.MirrorCS", {"start": v(3.27, 16.05) * mm, "end": v(3.47, 24.05) * mm});
            skLineSegment(sketch, "E186.MirrorCS", {"start": v(-0.73, 16.15) * mm, "end": v(3.27, 16.05) * mm});
            skPoint(sketch, "E187", {"position": v(80, 88.56) * mm});
            skLineSegment(sketch, "E188", {"start": v(0, 83.56) * mm, "end": v(4, 83.56) * mm});
            skLineSegment(sketch, "E189", {"start": v(4, 83.56) * mm, "end": v(4, 88.56) * mm});
            skLineSegment(sketch, "E190.MirrorCS", {"start": v(80, 83.56) * mm, "end": v(76, 83.56) * mm});
            skLineSegment(sketch, "E191.MirrorCS", {"start": v(76, 83.56) * mm, "end": v(76, 88.56) * mm});
            skSolve(sketch);
        }
        {
            var Q0;
            Q0=sQuery(id+"F2.wireOp",EDGE,"E5");
            cPlane(context, id + "F16", {"entities" : qUnion([Q0]), "cplaneType" : CPlaneType.LINE_ANGLE, "offset" : 25 * mm, "angle" : 0 * degree, "width" : 150 * mm, "height" : 150 * mm});
        }
        {
            var Q0;
            Q0=qCreatedBy(id+"F16.planeOp",FACE);
            var sketch = newSketch(context, id + "F17", { "sketchPlane" : qUnion([Q0])});
            skLineSegment(sketch, "E192.0", {"start": v(0, 152.42) * mm, "end": v(0, 220.42) * mm});
            skLineSegment(sketch, "E193", {"start": v(0, 153.58) * mm, "end": v(80, 153.58) * mm});
            skLineSegment(sketch, "E194", {"start": v(0, 218.42) * mm, "end": v(80, 218.42) * mm});
            skLineSegment(sketch, "E195", {"start": v(80, 218.42) * mm, "end": v(80, 153.58) * mm});
            skLineSegment(sketch, "E196", {"start": v(0, 186.42) * mm, "end": v(80, 186.42) * mm, "construction": true});
            skLineSegment(sketch, "E197", {"start": v(80, 186.42) * mm, "end": v(0, 218.42) * mm, "construction": true});
            skLineSegment(sketch, "E198", {"start": v(40, 202.42) * mm, "end": v(0, 202.42) * mm, "construction": true});
            skLineSegment(sketch, "E199", {"start": v(0, 191.42) * mm, "end": v(4, 191.42) * mm});
            skLineSegment(sketch, "E200", {"start": v(4, 191.42) * mm, "end": v(4, 186.42) * mm});
            skLineSegment(sketch, "E201.MirrorCS", {"start": v(4, 181.42) * mm, "end": v(4, 186.42) * mm});
            skLineSegment(sketch, "E202.MirrorCS", {"start": v(0, 181.42) * mm, "end": v(4, 181.42) * mm});
            skLineSegment(sketch, "E203", {"start": v(0, 207.42) * mm, "end": v(4, 207.42) * mm});
            skLineSegment(sketch, "E204", {"start": v(4, 207.42) * mm, "end": v(4, 202.42) * mm});
            skLineSegment(sketch, "E205.MirrorCS", {"start": v(4, 197.42) * mm, "end": v(4, 202.42) * mm});
            skLineSegment(sketch, "E206.MirrorCS", {"start": v(0, 197.42) * mm, "end": v(4, 197.42) * mm});
            skLineSegment(sketch, "E207.MirrorCS", {"start": v(4, 175.42) * mm, "end": v(4, 170.42) * mm});
            skLineSegment(sketch, "E208.MirrorCS", {"start": v(0, 175.42) * mm, "end": v(4, 175.42) * mm});
            skLineSegment(sketch, "E209.MirrorCS", {"start": v(4, 165.42) * mm, "end": v(4, 170.42) * mm});
            skLineSegment(sketch, "E210.MirrorCS", {"start": v(0, 165.42) * mm, "end": v(4, 165.42) * mm});
            skLineSegment(sketch, "E211", {"start": v(40, 202.42) * mm, "end": v(40, 174.67) * mm, "construction": true});
            skPoint(sketch, "E211.endSnap0", {"position": v(40, 186.42) * mm});
            skLineSegment(sketch, "E212.MirrorCS", {"start": v(80, 207.42) * mm, "end": v(76, 207.42) * mm});
            skLineSegment(sketch, "E213.MirrorCS", {"start": v(76, 207.42) * mm, "end": v(76, 202.42) * mm});
            skLineSegment(sketch, "E214.MirrorCS", {"start": v(76, 197.42) * mm, "end": v(76, 202.42) * mm});
            skLineSegment(sketch, "E215.MirrorCS", {"start": v(80, 197.42) * mm, "end": v(76, 197.42) * mm});
            skLineSegment(sketch, "E216.MirrorCS", {"start": v(80, 191.42) * mm, "end": v(76, 191.42) * mm});
            skLineSegment(sketch, "E217.MirrorCS", {"start": v(76, 191.42) * mm, "end": v(76, 186.42) * mm});
            skLineSegment(sketch, "E218.MirrorCS", {"start": v(76, 181.42) * mm, "end": v(76, 186.42) * mm});
            skLineSegment(sketch, "E219.MirrorCS", {"start": v(80, 181.42) * mm, "end": v(76, 181.42) * mm});
            skLineSegment(sketch, "E220.MirrorCS", {"start": v(80, 175.42) * mm, "end": v(76, 175.42) * mm});
            skLineSegment(sketch, "E221.MirrorCS", {"start": v(76, 175.42) * mm, "end": v(76, 170.42) * mm});
            skLineSegment(sketch, "E222.MirrorCS", {"start": v(76, 165.42) * mm, "end": v(76, 170.42) * mm});
            skLineSegment(sketch, "E223.MirrorCS", {"start": v(80, 165.42) * mm, "end": v(76, 165.42) * mm});
            skLineSegment(sketch, "E224", {"start": v(0, 213.42) * mm, "end": v(4, 213.42) * mm});
            skLineSegment(sketch, "E225", {"start": v(4, 213.42) * mm, "end": v(4, 218.42) * mm});
            skLineSegment(sketch, "E226.MirrorCS", {"start": v(76, 213.42) * mm, "end": v(76, 218.42) * mm});
            skLineSegment(sketch, "E227.MirrorCS", {"start": v(80, 213.42) * mm, "end": v(76, 213.42) * mm});
            skSolve(sketch);
        }
        {
            var Q0;
            Q0=sQuery(id+"F2.wireOp",EDGE,"E4");
            cPlane(context, id + "F18", {"entities" : qUnion([Q0]), "cplaneType" : CPlaneType.LINE_ANGLE, "offset" : 25 * mm, "angle" : 0 * degree, "width" : 150 * mm, "height" : 150 * mm});
        }
        {
            var Q0;
            Q0=qCreatedBy(id+"F18.planeOp",FACE);
            var sketch = newSketch(context, id + "F19", { "sketchPlane" : qUnion([Q0])});
            skLineSegment(sketch, "E228.0", {"start": v(0, 38.42) * mm, "end": v(0, 106.42) * mm});
            skLineSegment(sketch, "E228.1", {"start": v(0, 106.42) * mm, "end": v(0, 108.73) * mm});
            skLineSegment(sketch, "E229", {"start": v(0, 38.42) * mm, "end": v(80, 38.42) * mm});
            skLineSegment(sketch, "E230", {"start": v(80, 38.42) * mm, "end": v(80, 108.73) * mm});
            skLineSegment(sketch, "E231", {"start": v(80, 108.73) * mm, "end": v(0, 108.73) * mm});
            skLineSegment(sketch, "E232", {"start": v(80, 73.58) * mm, "end": v(0, 73.58) * mm, "construction": true});
            skLineSegment(sketch, "E233", {"start": v(0, 73.58) * mm, "end": v(80, 108.73) * mm, "construction": true});
            skLineSegment(sketch, "E234", {"start": v(40, 91.16) * mm, "end": v(0, 91.16) * mm, "construction": true});
            skLineSegment(sketch, "E235", {"start": v(0, 68.58) * mm, "end": v(4, 68.58) * mm});
            skLineSegment(sketch, "E236", {"start": v(4, 68.58) * mm, "end": v(4, 73.58) * mm});
            skLineSegment(sketch, "E237.MirrorCS", {"start": v(4, 78.58) * mm, "end": v(4, 73.58) * mm});
            skLineSegment(sketch, "E238.MirrorCS", {"start": v(0, 78.58) * mm, "end": v(4, 78.58) * mm});
            skLineSegment(sketch, "E239", {"start": v(0, 86.16) * mm, "end": v(4, 86.16) * mm});
            skPoint(sketch, "E239.endSnap0", {"position": v(4, 76.08) * mm});
            skLineSegment(sketch, "E240", {"start": v(4, 86.16) * mm, "end": v(4, 91.16) * mm});
            skLineSegment(sketch, "E241.MirrorCS", {"start": v(4, 96.16) * mm, "end": v(4, 91.16) * mm});
            skLineSegment(sketch, "E242.MirrorCS", {"start": v(0, 96.16) * mm, "end": v(4, 96.16) * mm});
            skLineSegment(sketch, "E243.MirrorCS", {"start": v(0, 61) * mm, "end": v(4, 61) * mm});
            skLineSegment(sketch, "E244.MirrorCS", {"start": v(4, 61) * mm, "end": v(4, 56) * mm});
            skLineSegment(sketch, "E245.MirrorCS", {"start": v(4, 51) * mm, "end": v(4, 56) * mm});
            skLineSegment(sketch, "E246.MirrorCS", {"start": v(0, 51) * mm, "end": v(4, 51) * mm});
            skLineSegment(sketch, "E247", {"start": v(40, 91.16) * mm, "end": v(40, 57) * mm, "construction": true});
            skLineSegment(sketch, "E248.MirrorCS", {"start": v(80, 51) * mm, "end": v(76, 51) * mm});
            skLineSegment(sketch, "E249.MirrorCS", {"start": v(76, 51) * mm, "end": v(76, 56) * mm});
            skLineSegment(sketch, "E250.MirrorCS", {"start": v(76, 61) * mm, "end": v(76, 56) * mm});
            skLineSegment(sketch, "E251.MirrorCS", {"start": v(80, 61) * mm, "end": v(76, 61) * mm});
            skLineSegment(sketch, "E252.MirrorCS", {"start": v(80, 68.58) * mm, "end": v(76, 68.58) * mm});
            skLineSegment(sketch, "E253.MirrorCS", {"start": v(76, 68.58) * mm, "end": v(76, 73.58) * mm});
            skLineSegment(sketch, "E254.MirrorCS", {"start": v(76, 78.58) * mm, "end": v(76, 73.58) * mm});
            skLineSegment(sketch, "E255.MirrorCS", {"start": v(80, 78.58) * mm, "end": v(76, 78.58) * mm});
            skLineSegment(sketch, "E256.MirrorCS", {"start": v(80, 86.16) * mm, "end": v(76, 86.16) * mm});
            skLineSegment(sketch, "E257.MirrorCS", {"start": v(76, 86.16) * mm, "end": v(76, 91.16) * mm});
            skLineSegment(sketch, "E258.MirrorCS", {"start": v(76, 96.16) * mm, "end": v(76, 91.16) * mm});
            skLineSegment(sketch, "E259.MirrorCS", {"start": v(80, 96.16) * mm, "end": v(76, 96.16) * mm});
            skCircle(sketch, "E260", {"center": v(40, 73.58) * mm, "radius": 25 * mm});
            skLineSegment(sketch, "E261", {"start": v(80, 103.73) * mm, "end": v(76, 103.73) * mm});
            skLineSegment(sketch, "E262", {"start": v(76, 103.73) * mm, "end": v(76, 108.73) * mm});
            skLineSegment(sketch, "E263.MirrorCS", {"start": v(0, 103.73) * mm, "end": v(4, 103.73) * mm});
            skLineSegment(sketch, "E264.MirrorCS", {"start": v(4, 103.73) * mm, "end": v(4, 108.73) * mm});
            skSolve(sketch);
        }
        {
            var Q0;
            Q0=qCreatedBy(id+"F6.planeOp",FACE);
            cPlane(context, id + "F20", {"entities" : qUnion([Q0]), "cplaneType" : CPlaneType.OFFSET, "offset" : (getVariable(context, 'HD')) * mm, "width" : 150 * mm, "height" : 150 * mm});
        }
        {
            var Q0;
            Q0=qCreatedBy(id+"F20.planeOp",FACE);
            cPlane(context, id + "F21", {"entities" : qUnion([Q0]), "cplaneType" : CPlaneType.OFFSET, "offset" : (getVariable(context, 'WT')) * 2 * mm, "width" : 150 * mm, "height" : 150 * mm});
        }
        {
            var Q0;
            Q0=qCreatedBy(id+"F21.planeOp",FACE);
            var sketch = newSketch(context, id + "F22", { "sketchPlane" : qUnion([Q0])});
            skLineSegment(sketch, "E265.0", {"start": v(0, 0) * mm, "end": v(0, 240) * mm});
            skLineSegment(sketch, "E265.1", {"start": v(80, 240) * mm, "end": v(0, 240) * mm});
            skLineSegment(sketch, "E265.2", {"start": v(80, 240) * mm, "end": v(80, 0) * mm});
            skLineSegment(sketch, "E265.3", {"start": v(80, 0) * mm, "end": v(0, 0) * mm});
            skCircle(sketch, "E265.4", {"center": v(9, 231) * mm, "radius": 3 * mm});
            skCircle(sketch, "E265.5", {"center": v(71, 231) * mm, "radius": 3 * mm});
            skCircle(sketch, "E265.6", {"center": v(9, 9) * mm, "radius": 3 * mm});
            skCircle(sketch, "E265.7", {"center": v(71, 9) * mm, "radius": 3 * mm});
            skLineSegment(sketch, "E266.0.1.0", {"start": v(0, 240) * mm, "end": v(0, 480) * mm});
            skCircle(sketch, "E266.0.1.1", {"center": v(9, 249) * mm, "radius": 3 * mm});
            skCircle(sketch, "E266.0.1.2", {"center": v(71, 249) * mm, "radius": 3 * mm});
            skLineSegment(sketch, "E266.0.1.3", {"start": v(80, 480) * mm, "end": v(80, 240) * mm});
            skCircle(sketch, "E266.0.1.4", {"center": v(9, 471) * mm, "radius": 3 * mm});
            skCircle(sketch, "E266.0.1.5", {"center": v(71, 471) * mm, "radius": 3 * mm});
            skLineSegment(sketch, "E266.0.1.6", {"start": v(80, 480) * mm, "end": v(0, 480) * mm});
            skLineSegment(sketch, "E266.0.2.0", {"start": v(0, 480) * mm, "end": v(0, 720) * mm});
            skCircle(sketch, "E266.0.2.1", {"center": v(9, 489) * mm, "radius": 3 * mm});
            skCircle(sketch, "E266.0.2.2", {"center": v(71, 489) * mm, "radius": 3 * mm});
            skLineSegment(sketch, "E266.0.2.3", {"start": v(80, 720) * mm, "end": v(80, 480) * mm});
            skCircle(sketch, "E266.0.2.4", {"center": v(9, 711) * mm, "radius": 3 * mm});
            skCircle(sketch, "E266.0.2.5", {"center": v(71, 711) * mm, "radius": 3 * mm});
            skLineSegment(sketch, "E266.0.2.6", {"start": v(80, 720) * mm, "end": v(0, 720) * mm});
            skLineSegment(sketch, "E266.0.3.0", {"start": v(0, 720) * mm, "end": v(0, 960) * mm});
            skCircle(sketch, "E266.0.3.1", {"center": v(9, 729) * mm, "radius": 3 * mm});
            skCircle(sketch, "E266.0.3.2", {"center": v(71, 729) * mm, "radius": 3 * mm});
            skLineSegment(sketch, "E266.0.3.3", {"start": v(80, 960) * mm, "end": v(80, 720) * mm});
            skCircle(sketch, "E266.0.3.4", {"center": v(9, 951) * mm, "radius": 3 * mm});
            skCircle(sketch, "E266.0.3.5", {"center": v(71, 951) * mm, "radius": 3 * mm});
            skLineSegment(sketch, "E266.0.3.6", {"start": v(80, 960) * mm, "end": v(0, 960) * mm});
            skLineSegment(sketch, "E266.direction1", {"start": v(0, 0) * mm, "end": v(25, 0) * mm, "construction": true});
            skLineSegment(sketch, "E266.direction2", {"start": v(0, 0) * mm, "end": v(0, 240) * mm, "construction": true});
            skSolve(sketch);
        }
        {
            var Q0;
            Q0=qCreatedBy(id+"F8.planeOp",FACE);
            var sketch = newSketch(context, id + "F23", { "sketchPlane" : qUnion([Q0])});
            skLineSegment(sketch, "E267.0", {"start": v(-80, 80) * mm, "end": v(0, 80) * mm});
            skLineSegment(sketch, "E267.1", {"start": v(-80, 0) * mm, "end": v(-80, 80) * mm});
            skLineSegment(sketch, "E267.2", {"start": v(-80, 0) * mm, "end": v(0, 0) * mm});
            skLineSegment(sketch, "E268", {"start": v(0, 80) * mm, "end": v(12, 80) * mm});
            skLineSegment(sketch, "E269", {"start": v(12, 80) * mm, "end": v(12, 0) * mm});
            skLineSegment(sketch, "E270", {"start": v(12, 0) * mm, "end": v(0, 0) * mm});
            skCircle(sketch, "E271.0", {"center": v(-70, 70) * mm, "radius": 3 * mm});
            skCircle(sketch, "E272.0", {"center": v(-70, 10) * mm, "radius": 3 * mm});
            skCircle(sketch, "E273.0", {"center": v(-10, 40) * mm, "radius": 3 * mm});
            skLineSegment(sketch, "E274.0", {"start": v(-40, 60) * mm, "end": v(-71, 60) * mm});
            skLineSegment(sketch, "E274.1", {"start": v(-71, 20) * mm, "end": v(-71, 60) * mm});
            skLineSegment(sketch, "E274.2", {"start": v(-40, 20) * mm, "end": v(-71, 20) * mm});
            skLineSegment(sketch, "E274.3", {"start": v(-40, 20) * mm, "end": v(-40, 60) * mm});
            skLineSegment(sketch, "E275", {"start": v(-31, 76) * mm, "end": v(-31, 4) * mm});
            skLineSegment(sketch, "E276", {"start": v(-31, 60) * mm, "end": v(-40, 60) * mm, "construction": true});
            skLineSegment(sketch, "E277", {"start": v(-71, 60) * mm, "end": v(-80, 60) * mm, "construction": true});
            skLineSegment(sketch, "E278", {"start": v(-27, 4) * mm, "end": v(-27, 76) * mm});
            skLineSegment(sketch, "E279.0", {"start": v(-80, 76) * mm, "end": v(0, 76) * mm});
            skLineSegment(sketch, "E280.0", {"start": v(-80, 4) * mm, "end": v(0, 4) * mm});
            skLineSegment(sketch, "E281.0", {"start": v(-76, 80) * mm, "end": v(-76, 0) * mm});
            skLineSegment(sketch, "E282.0", {"start": v(-10, 80) * mm, "end": v(-10, 76) * mm});
            skLineSegment(sketch, "E282.1", {"start": v(-20, 80) * mm, "end": v(-20, 76) * mm});
            skLineSegment(sketch, "E282.2", {"start": v(-30, 80) * mm, "end": v(-30, 76) * mm});
            skLineSegment(sketch, "E282.3", {"start": v(-40, 80) * mm, "end": v(-40, 76) * mm});
            skLineSegment(sketch, "E282.4", {"start": v(-50, 80) * mm, "end": v(-50, 76) * mm});
            skLineSegment(sketch, "E282.5", {"start": v(-60, 80) * mm, "end": v(-60, 76) * mm});
            skLineSegment(sketch, "E282.6", {"start": v(-70, 80) * mm, "end": v(-70, 76) * mm});
            skLineSegment(sketch, "E283.0", {"start": v(-80, 71.1) * mm, "end": v(-76, 71.1) * mm});
            skLineSegment(sketch, "E283.1", {"start": v(-80, 62.34) * mm, "end": v(-76, 62.34) * mm});
            skLineSegment(sketch, "E283.2", {"start": v(-80, 53.6) * mm, "end": v(-76, 53.6) * mm});
            skLineSegment(sketch, "E283.3", {"start": v(-80, 44.84) * mm, "end": v(-76, 44.84) * mm});
            skLineSegment(sketch, "E283.4", {"start": v(-80, 36.1) * mm, "end": v(-76, 36.1) * mm});
            skLineSegment(sketch, "E283.5", {"start": v(-80, 27.34) * mm, "end": v(-76, 27.34) * mm});
            skLineSegment(sketch, "E283.6", {"start": v(-80, 18.6) * mm, "end": v(-76, 18.6) * mm});
            skLineSegment(sketch, "E284.0", {"start": v(-70, 0) * mm, "end": v(-70, 4) * mm});
            skLineSegment(sketch, "E285.0", {"start": v(-60, 0) * mm, "end": v(-60, 4) * mm});
            skLineSegment(sketch, "E285.1", {"start": v(-50, 0) * mm, "end": v(-50, 4) * mm});
            skLineSegment(sketch, "E285.2", {"start": v(-40, 0) * mm, "end": v(-40, 4) * mm});
            skLineSegment(sketch, "E285.3", {"start": v(-30, 0) * mm, "end": v(-30, 4) * mm});
            skLineSegment(sketch, "E285.4", {"start": v(-20, 0) * mm, "end": v(-20, 4) * mm});
            skLineSegment(sketch, "E285.5", {"start": v(-10, 0) * mm, "end": v(-10, 4) * mm});
            skLineSegment(sketch, "E286", {"start": v(0, 76) * mm, "end": v(12, 76) * mm});
            skLineSegment(sketch, "E287", {"start": v(8, 80) * mm, "end": v(8, 0) * mm});
            skLineSegment(sketch, "E288", {"start": v(0, 4) * mm, "end": v(12, 4) * mm});
            skLineSegment(sketch, "E289.0", {"start": v(0, 71.1) * mm, "end": v(-4, 71.1) * mm, "construction": true});
            skLineSegment(sketch, "E290", {"start": v(8, 71.1) * mm, "end": v(12, 71.1) * mm});
            skLineSegment(sketch, "E291", {"start": v(8, 62.34) * mm, "end": v(12, 62.34) * mm});
            skLineSegment(sketch, "E292", {"start": v(8, 53.6) * mm, "end": v(12, 53.6) * mm});
            skLineSegment(sketch, "E293", {"start": v(8, 44.84) * mm, "end": v(12, 44.84) * mm});
            skLineSegment(sketch, "E294", {"start": v(8, 27.34) * mm, "end": v(12, 27.34) * mm});
            skLineSegment(sketch, "E295", {"start": v(8, 18.6) * mm, "end": v(12, 18.6) * mm});
            skLineSegment(sketch, "E296", {"start": v(8, 36.1) * mm, "end": v(12, 36.1) * mm});
            skLineSegment(sketch, "E297.0", {"start": v(-80, 9.84) * mm, "end": v(-76, 9.84) * mm});
            skLineSegment(sketch, "E298", {"start": v(8, 9.84) * mm, "end": v(12, 9.68) * mm});
            skSolve(sketch);
        }
        {
            var Q0;
            Q0=qCreatedBy(id+"F8.planeOp",FACE);
            var sketch = newSketch(context, id + "F24", { "sketchPlane" : qUnion([Q0])});
            skLineSegment(sketch, "E299.0", {"start": v(-80, 80) * mm, "end": v(0, 80) * mm});
            skLineSegment(sketch, "E299.1", {"start": v(-80, 0) * mm, "end": v(-80, 80) * mm});
            skLineSegment(sketch, "E299.2", {"start": v(-80, 0) * mm, "end": v(0, 0) * mm});
            skLineSegment(sketch, "E299.3", {"start": v(12, 0) * mm, "end": v(0, 0) * mm});
            skLineSegment(sketch, "E299.4", {"start": v(12, 80) * mm, "end": v(12, 0) * mm});
            skLineSegment(sketch, "E299.5", {"start": v(0, 80) * mm, "end": v(12, 80) * mm});
            skCircle(sketch, "E300.0", {"center": v(-70, 70) * mm, "radius": 3 * mm});
            skLineSegment(sketch, "E300.1", {"start": v(-40, 60) * mm, "end": v(-71, 60) * mm});
            skLineSegment(sketch, "E300.2", {"start": v(-71, 20) * mm, "end": v(-71, 60) * mm});
            skLineSegment(sketch, "E300.3", {"start": v(-40, 20) * mm, "end": v(-71, 20) * mm});
            skLineSegment(sketch, "E300.4", {"start": v(-40, 20) * mm, "end": v(-40, 60) * mm});
            skCircle(sketch, "E300.5", {"center": v(-70, 10) * mm, "radius": 3 * mm});
            skCircle(sketch, "E301.0", {"center": v(-10, 40) * mm, "radius": 3 * mm});
            skSolve(sketch);
        }
        {
            var Q0;
            {var subQ0=sQuery(id+"F5.wireOp",EDGE,"E50");Q0=makeQuery(id+"F5.imprint","IMPRINT",FACE,{"disambiguationData":[TD([[makeQuery(id+"F5.imprint","IMPRINT",EDGE,{"derivedFrom":subQ0}),-1.0]])]});}
            var Q1;
            {var subQ0=sQuery(id+"F5.wireOp",EDGE,"E51.1.0.0");Q1=makeQuery(id+"F5.imprint","IMPRINT",FACE,{"disambiguationData":[TD([[makeQuery(id+"F5.imprint","IMPRINT",EDGE,{"derivedFrom":subQ0}),1.0]])]});}
            var Q2;
            {var subQ0=sQuery(id+"F5.wireOp",EDGE,"E51.3.0.0");Q2=makeQuery(id+"F5.imprint","IMPRINT",FACE,{"disambiguationData":[TD([[makeQuery(id+"F5.imprint","IMPRINT",EDGE,{"derivedFrom":subQ0}),1.0]])]});}
            var Q3;
            {var subQ0=sQuery(id+"F5.wireOp",EDGE,"E51.5.0.0");Q3=makeQuery(id+"F5.imprint","IMPRINT",FACE,{"disambiguationData":[TD([[makeQuery(id+"F5.imprint","IMPRINT",EDGE,{"derivedFrom":subQ0}),1.0]])]});}
            var Q4;
            {var subQ0=sQuery(id+"F5.wireOp",EDGE,"E47");var subQ1=sQuery(id+"F5.wireOp",EDGE,"E46");var subQ2=makeQuery(id+"F5.imprint","INTERSECT",VERTEX,{"derivedFrom":[subQ1,subQ0]});Q4=makeQuery(id+"F5.imprint","IMPRINT",FACE,{"disambiguationData":[TD([[makeQuery(id+"F5.imprint","IMPRINT",EDGE,{"disambiguationData":[TD([[subQ2,1.0]])],"derivedFrom":subQ1}),-1.0]])]});}
            var Q5;
            {var subQ3=sQuery(id+"F5.wireOp",EDGE,"E70.MirrorCS");Q5=makeQuery(id+"F5.imprint","IMPRINT",FACE,{"disambiguationData":[TD([[makeQuery(id+"F5.imprint","IMPRINT",EDGE,{"derivedFrom":subQ3}),-1.0]])]});}
            var Q6;
            {var subQ0=sQuery(id+"F5.wireOp",EDGE,"E68.MirrorCS");Q6=makeQuery(id+"F5.imprint","IMPRINT",FACE,{"disambiguationData":[TD([[makeQuery(id+"F5.imprint","IMPRINT",EDGE,{"derivedFrom":subQ0}),-1.0]])]});}
            var Q7;
            {var subQ0=sQuery(id+"F5.wireOp",EDGE,"E66.MirrorCS");Q7=makeQuery(id+"F5.imprint","IMPRINT",FACE,{"disambiguationData":[TD([[makeQuery(id+"F5.imprint","IMPRINT",EDGE,{"derivedFrom":subQ0}),-1.0]])]});}
            var Q8;
            {var subQ0=sQuery(id+"F5.wireOp",EDGE,"E64.MirrorCS");Q8=makeQuery(id+"F5.imprint","IMPRINT",FACE,{"disambiguationData":[TD([[makeQuery(id+"F5.imprint","IMPRINT",EDGE,{"derivedFrom":subQ0}),-1.0]])]});}
            var Q9;
            {var subQ0=sQuery(id+"F5.wireOp",EDGE,"E57.MirrorCS");Q9=makeQuery(id+"F5.imprint","IMPRINT",FACE,{"disambiguationData":[TD([[makeQuery(id+"F5.imprint","IMPRINT",EDGE,{"derivedFrom":subQ0}),-1.0]])]});}
            var Q10;
            {var subQ0=sQuery(id+"F5.wireOp",EDGE,"E55.MirrorCS");Q10=makeQuery(id+"F5.imprint","IMPRINT",FACE,{"disambiguationData":[TD([[makeQuery(id+"F5.imprint","IMPRINT",EDGE,{"derivedFrom":subQ0}),-1.0]])]});}
            var Q11;
            {var subQ0=sQuery(id+"F5.wireOp",EDGE,"E53.MirrorCS");Q11=makeQuery(id+"F5.imprint","IMPRINT",FACE,{"disambiguationData":[TD([[makeQuery(id+"F5.imprint","IMPRINT",EDGE,{"derivedFrom":subQ0}),-1.0]])]});}
            var Q12;
            {var subQ0=sQuery(id+"F5.wireOp",EDGE,"E61");Q12=makeQuery(id+"F5.imprint","IMPRINT",FACE,{"disambiguationData":[TD([[makeQuery(id+"F5.imprint","IMPRINT",EDGE,{"derivedFrom":subQ0}),-1.0]])]});}
            var Q13;
            {var subQ0=sQuery(id+"F5.wireOp",EDGE,"E62.0.2.0");Q13=makeQuery(id+"F5.imprint","IMPRINT",FACE,{"disambiguationData":[TD([[makeQuery(id+"F5.imprint","IMPRINT",EDGE,{"derivedFrom":subQ0}),-1.0]])]});}
            var Q14;
            {var subQ0=sQuery(id+"F5.wireOp",EDGE,"E62.0.4.0");Q14=makeQuery(id+"F5.imprint","IMPRINT",FACE,{"disambiguationData":[TD([[makeQuery(id+"F5.imprint","IMPRINT",EDGE,{"derivedFrom":subQ0}),-1.0]])]});}
            var Q15;
            {var subQ3=sQuery(id+"F5.wireOp",EDGE,"E62.0.6.0");Q15=makeQuery(id+"F5.imprint","IMPRINT",FACE,{"disambiguationData":[TD([[makeQuery(id+"F5.imprint","IMPRINT",EDGE,{"derivedFrom":subQ3}),-1.0]])]});}
            var Q16;
            {var subQ7=sQuery(id+"F5.wireOp",EDGE,"E49");var subQ21=makeQuery(id+"F5.imprint","INTERSECT",VERTEX,{"derivedFrom":[subQ7,sQuery(id+"F5.wireOp",EDGE,"E50")]});Q16=makeQuery(id+"F5.imprint","IMPRINT",FACE,{"disambiguationData":[TD([[makeQuery(id+"F5.imprint","IMPRINT",EDGE,{"disambiguationData":[TD([[subQ21,1.0]])],"derivedFrom":subQ7}),-1.0]])]});}
            var Q17;
            {var subQ3=sQuery(id+"F5.wireOp",EDGE,"E79.MirrorCS");Q17=makeQuery(id+"F5.imprint","IMPRINT",FACE,{"disambiguationData":[TD([[makeQuery(id+"F5.imprint","IMPRINT",EDGE,{"derivedFrom":subQ3}),1.0]])]});}
            var Q18;
            {var subQ0=sQuery(id+"F5.wireOp",EDGE,"E59.MirrorCS");Q18=makeQuery(id+"F5.imprint","IMPRINT",FACE,{"disambiguationData":[TD([[makeQuery(id+"F5.imprint","IMPRINT",EDGE,{"derivedFrom":subQ0}),-1.0]])]});}
            var Q19;
            {var subQ0=sQuery(id+"F5.wireOp",EDGE,"E45");var subQ1=sQuery(id+"F5.wireOp",EDGE,"E44.0");var subQ2=makeQuery(id+"F5.imprint","INTERSECT",VERTEX,{"derivedFrom":[subQ1,subQ0]});Q19=makeQuery(id+"F5.imprint","IMPRINT",FACE,{"disambiguationData":[TD([[makeQuery(id+"F5.imprint","IMPRINT",EDGE,{"disambiguationData":[TD([[subQ2,-1.0]])],"derivedFrom":subQ1}),1.0]])]});}
            var Q20;
            {var subQ0=sQuery(id+"F5.wireOp",EDGE,"E53.MirrorCS");Q20=makeQuery(id+"F5.imprint","IMPRINT",FACE,{"disambiguationData":[TD([[makeQuery(id+"F5.imprint","IMPRINT",EDGE,{"derivedFrom":subQ0}),1.0]])]});}
            extrude(context, id + "F25", {"entities" : qUnion([Q0, Q1, Q2, Q3, Q4, Q5, Q6, Q7, Q8, Q9, Q10, Q11, Q12, Q13, Q14, Q15, Q16, Q17, Q18, Q19, Q20]), "oppositeDirection" : true, "depth" : getVariable(context, 'WT') * mm});
        }
        {
            var Q0;
            {var subQ0=sQuery(id+"F7.wireOp",EDGE,"E84");var subQ9=sQuery(id+"F7.wireOp",EDGE,"E81.0");var subQ10=makeQuery(id+"F7.imprint","INTERSECT",VERTEX,{"derivedFrom":[subQ9,subQ0]});Q0=makeQuery(id+"F7.imprint","IMPRINT",FACE,{"disambiguationData":[TD([[makeQuery(id+"F7.imprint","IMPRINT",EDGE,{"disambiguationData":[TD([[subQ10,1.0]])],"derivedFrom":subQ9}),1.0]])]});}
            var Q1;
            {var subQ3=sQuery(id+"F7.wireOp",EDGE,"E85");Q1=makeQuery(id+"F7.imprint","IMPRINT",FACE,{"disambiguationData":[TD([[makeQuery(id+"F7.imprint","IMPRINT",EDGE,{"derivedFrom":subQ3}),1.0]])]});}
            var Q2;
            {var subQ0=sQuery(id+"F7.wireOp",EDGE,"E86.0.1.0");Q2=makeQuery(id+"F7.imprint","IMPRINT",FACE,{"disambiguationData":[TD([[makeQuery(id+"F7.imprint","IMPRINT",EDGE,{"derivedFrom":subQ0}),-1.0]])]});}
            var Q3;
            {var subQ0=sQuery(id+"F7.wireOp",EDGE,"E86.0.3.0");Q3=makeQuery(id+"F7.imprint","IMPRINT",FACE,{"disambiguationData":[TD([[makeQuery(id+"F7.imprint","IMPRINT",EDGE,{"derivedFrom":subQ0}),-1.0]])]});}
            var Q4;
            {var subQ0=sQuery(id+"F7.wireOp",EDGE,"E86.0.5.0");Q4=makeQuery(id+"F7.imprint","IMPRINT",FACE,{"disambiguationData":[TD([[makeQuery(id+"F7.imprint","IMPRINT",EDGE,{"derivedFrom":subQ0}),-1.0]])]});}
            var Q5;
            {var subQ3=sQuery(id+"F7.wireOp",EDGE,"E95.MirrorCS");Q5=makeQuery(id+"F7.imprint","IMPRINT",FACE,{"disambiguationData":[TD([[makeQuery(id+"F7.imprint","IMPRINT",EDGE,{"derivedFrom":subQ3}),1.0]])]});}
            var Q6;
            {var subQ0=sQuery(id+"F7.wireOp",EDGE,"E93.MirrorCS");Q6=makeQuery(id+"F7.imprint","IMPRINT",FACE,{"disambiguationData":[TD([[makeQuery(id+"F7.imprint","IMPRINT",EDGE,{"derivedFrom":subQ0}),1.0]])]});}
            var Q7;
            {var subQ0=sQuery(id+"F7.wireOp",EDGE,"E91.MirrorCS");Q7=makeQuery(id+"F7.imprint","IMPRINT",FACE,{"disambiguationData":[TD([[makeQuery(id+"F7.imprint","IMPRINT",EDGE,{"derivedFrom":subQ0}),1.0]])]});}
            var Q8;
            {var subQ0=sQuery(id+"F7.wireOp",EDGE,"E89.MirrorCS");Q8=makeQuery(id+"F7.imprint","IMPRINT",FACE,{"disambiguationData":[TD([[makeQuery(id+"F7.imprint","IMPRINT",EDGE,{"derivedFrom":subQ0}),1.0]])]});}
            extrude(context, id + "F26", {"entities" : qUnion([Q0, Q1, Q2, Q3, Q4, Q5, Q6, Q7, Q8]), "oppositeDirection" : true, "depth" : (getVariable(context, 'WT')) * mm});
        }
        {
            var Q0;
            Q0=makeQuery(id+"F3.imprint","IMPRINT",FACE,{"disambiguationData":[TD([[makeQuery(id+"F3.imprint","IMPRINT",EDGE,{"derivedFrom":sQuery(id+"F3.wireOp",EDGE,"E37.0")}),-1.0]])]});
            extrude(context, id + "F27", {"entities" : qUnion([Q0]), "oppositeDirection" : true, "depth" : (getVariable(context, 'WT')) * mm});
        }
        {
            var Q0;
            {var subQ3=sQuery(id+"F9.wireOp",EDGE,"E101.21");Q0=makeQuery(id+"F9.imprint","IMPRINT",FACE,{"disambiguationData":[TD([[makeQuery(id+"F9.imprint","IMPRINT",EDGE,{"derivedFrom":subQ3}),-1.0]])]});}
            var Q1;
            {var subQ0=sQuery(id+"F9.wireOp",EDGE,"E101.22");Q1=makeQuery(id+"F9.imprint","IMPRINT",FACE,{"disambiguationData":[TD([[makeQuery(id+"F9.imprint","IMPRINT",EDGE,{"derivedFrom":subQ0}),1.0]])]});}
            var Q2;
            {var subQ0=sQuery(id+"F9.wireOp",EDGE,"E101.24");Q2=makeQuery(id+"F9.imprint","IMPRINT",FACE,{"disambiguationData":[TD([[makeQuery(id+"F9.imprint","IMPRINT",EDGE,{"derivedFrom":subQ0}),1.0]])]});}
            var Q3;
            {var subQ0=sQuery(id+"F9.wireOp",EDGE,"E101.26");Q3=makeQuery(id+"F9.imprint","IMPRINT",FACE,{"disambiguationData":[TD([[makeQuery(id+"F9.imprint","IMPRINT",EDGE,{"derivedFrom":subQ0}),1.0]])]});}
            var Q4;
            {var subQ4=sQuery(id+"F9.wireOp",EDGE,"E101.4");var subQ23=makeQuery(id+"F9.imprint","INTERSECT",VERTEX,{"derivedFrom":[subQ4,sQuery(id+"F9.wireOp",EDGE,"E101.7")]});Q4=makeQuery(id+"F9.imprint","IMPRINT",FACE,{"disambiguationData":[TD([[makeQuery(id+"F9.imprint","IMPRINT",EDGE,{"disambiguationData":[TD([[subQ23,1.0]])],"derivedFrom":subQ4}),-1.0]])]});}
            var Q5;
            {var subQ3=sQuery(id+"F9.wireOp",EDGE,"E101.28");Q5=makeQuery(id+"F9.imprint","IMPRINT",FACE,{"disambiguationData":[TD([[makeQuery(id+"F9.imprint","IMPRINT",EDGE,{"derivedFrom":subQ3}),-1.0]])]});}
            var Q6;
            {var subQ0=sQuery(id+"F9.wireOp",EDGE,"E101.29");Q6=makeQuery(id+"F9.imprint","IMPRINT",FACE,{"disambiguationData":[TD([[makeQuery(id+"F9.imprint","IMPRINT",EDGE,{"derivedFrom":subQ0}),1.0]])]});}
            var Q7;
            {var subQ0=sQuery(id+"F9.wireOp",EDGE,"E101.18");Q7=makeQuery(id+"F9.imprint","IMPRINT",FACE,{"disambiguationData":[TD([[makeQuery(id+"F9.imprint","IMPRINT",EDGE,{"derivedFrom":subQ0}),1.0]])]});}
            var Q8;
            {var subQ0=sQuery(id+"F9.wireOp",EDGE,"E101.17");Q8=makeQuery(id+"F9.imprint","IMPRINT",FACE,{"disambiguationData":[TD([[makeQuery(id+"F9.imprint","IMPRINT",EDGE,{"derivedFrom":subQ0}),-1.0]])]});}
            var Q9;
            {var subQ0=sQuery(id+"F9.wireOp",EDGE,"E101.15");Q9=makeQuery(id+"F9.imprint","IMPRINT",FACE,{"disambiguationData":[TD([[makeQuery(id+"F9.imprint","IMPRINT",EDGE,{"derivedFrom":subQ0}),1.0]])]});}
            var Q10;
            {var subQ3=sQuery(id+"F9.wireOp",EDGE,"E101.14");Q10=makeQuery(id+"F9.imprint","IMPRINT",FACE,{"disambiguationData":[TD([[makeQuery(id+"F9.imprint","IMPRINT",EDGE,{"derivedFrom":subQ3}),-1.0]])]});}
            var Q11;
            {var subQ0=sQuery(id+"F9.wireOp",EDGE,"E101.3");var subQ1=sQuery(id+"F9.wireOp",EDGE,"E101.1");var subQ2=makeQuery(id+"F9.imprint","INTERSECT",VERTEX,{"derivedFrom":[subQ1,subQ0]});Q11=makeQuery(id+"F9.imprint","IMPRINT",FACE,{"disambiguationData":[TD([[makeQuery(id+"F9.imprint","IMPRINT",EDGE,{"disambiguationData":[TD([[subQ2,-1.0]])],"derivedFrom":subQ1}),-1.0]])]});}
            var Q12;
            {var subQ0=sQuery(id+"F9.wireOp",EDGE,"E101.12");Q12=makeQuery(id+"F9.imprint","IMPRINT",FACE,{"disambiguationData":[TD([[makeQuery(id+"F9.imprint","IMPRINT",EDGE,{"derivedFrom":subQ0}),1.0]])]});}
            var Q13;
            {var subQ0=sQuery(id+"F9.wireOp",EDGE,"E101.10");Q13=makeQuery(id+"F9.imprint","IMPRINT",FACE,{"disambiguationData":[TD([[makeQuery(id+"F9.imprint","IMPRINT",EDGE,{"derivedFrom":subQ0}),1.0]])]});}
            var Q14;
            {var subQ0=sQuery(id+"F9.wireOp",EDGE,"E101.8");Q14=makeQuery(id+"F9.imprint","IMPRINT",FACE,{"disambiguationData":[TD([[makeQuery(id+"F9.imprint","IMPRINT",EDGE,{"derivedFrom":subQ0}),1.0]])]});}
            var Q15;
            {var subQ3=sQuery(id+"F9.wireOp",EDGE,"E101.7");Q15=makeQuery(id+"F9.imprint","IMPRINT",FACE,{"disambiguationData":[TD([[makeQuery(id+"F9.imprint","IMPRINT",EDGE,{"derivedFrom":subQ3}),-1.0]])]});}
            var Q16;
            {var subQ0=sQuery(id+"F9.wireOp",EDGE,"E101.33");Q16=makeQuery(id+"F9.imprint","IMPRINT",FACE,{"disambiguationData":[TD([[makeQuery(id+"F9.imprint","IMPRINT",EDGE,{"derivedFrom":subQ0}),1.0]])]});}
            var Q17;
            {var subQ0=sQuery(id+"F9.wireOp",EDGE,"E101.31");Q17=makeQuery(id+"F9.imprint","IMPRINT",FACE,{"disambiguationData":[TD([[makeQuery(id+"F9.imprint","IMPRINT",EDGE,{"derivedFrom":subQ0}),1.0]])]});}
            var Q18;
            {var subQ0=sQuery(id+"F9.wireOp",EDGE,"E101.2");var subQ1=sQuery(id+"F9.wireOp",EDGE,"E101.0");var subQ2=makeQuery(id+"F9.imprint","INTERSECT",VERTEX,{"derivedFrom":[subQ1,subQ0]});Q18=makeQuery(id+"F9.imprint","IMPRINT",FACE,{"disambiguationData":[TD([[makeQuery(id+"F9.imprint","IMPRINT",EDGE,{"disambiguationData":[TD([[subQ2,-1.0]])],"derivedFrom":subQ1}),1.0]])]});}
            extrude(context, id + "F28", {"entities" : qUnion([Q0, Q1, Q2, Q3, Q4, Q5, Q6, Q7, Q8, Q9, Q10, Q11, Q12, Q13, Q14, Q15, Q16, Q17, Q18]), "depth" : (getVariable(context, 'WT')) * mm});
        }
        {
            var Q0;
            Q0=makeQuery(id+"F11.imprint","IMPRINT",FACE,{"disambiguationData":[TD([[makeQuery(id+"F11.imprint","IMPRINT",EDGE,{"derivedFrom":sQuery(id+"F11.wireOp",EDGE,"E117.0")}),1.0]])]});
            extrude(context, id + "F29", {"entities" : qUnion([Q0]), "oppositeDirection" : true, "depth" : (getVariable(context, 'WT')) * mm});
        }
        {
            var Q0;
            {var subQ4=sQuery(id+"F13.wireOp",EDGE,"E124.0");Q0=makeQuery(id+"F13.imprint","IMPRINT",FACE,{"disambiguationData":[TD([[makeQuery(id+"F13.imprint","IMPRINT",EDGE,{"derivedFrom":subQ4}),-1.0]])]});}
            extrude(context, id + "F30", {"entities" : qUnion([Q0]), "depth" : (getVariable(context, 'WT')) * mm});
        }
        {
            var Q0;
            {var subQ9=sQuery(id+"F15.wireOp",EDGE,"E156.0");Q0=makeQuery(id+"F15.imprint","IMPRINT",FACE,{"disambiguationData":[TD([[makeQuery(id+"F15.imprint","IMPRINT",EDGE,{"derivedFrom":subQ9}),1.0]])]});}
            extrude(context, id + "F31", {"entities" : qUnion([Q0]), "depth" : (getVariable(context, 'WT')) * mm});
        }
        {
            var Q0;
            {var subQ0=sQuery(id+"F5.wireOp",EDGE,"E64.MirrorCS");Q0=makeQuery(id+"F5.imprint","IMPRINT",FACE,{"disambiguationData":[TD([[makeQuery(id+"F5.imprint","IMPRINT",EDGE,{"derivedFrom":subQ0}),-1.0]])]});}
            var Q1;
            {var subQ0=sQuery(id+"F5.wireOp",EDGE,"E66.MirrorCS");Q1=makeQuery(id+"F5.imprint","IMPRINT",FACE,{"disambiguationData":[TD([[makeQuery(id+"F5.imprint","IMPRINT",EDGE,{"derivedFrom":subQ0}),-1.0]])]});}
            var Q2;
            {var subQ0=sQuery(id+"F5.wireOp",EDGE,"E68.MirrorCS");Q2=makeQuery(id+"F5.imprint","IMPRINT",FACE,{"disambiguationData":[TD([[makeQuery(id+"F5.imprint","IMPRINT",EDGE,{"derivedFrom":subQ0}),-1.0]])]});}
            var Q3;
            {var subQ3=sQuery(id+"F5.wireOp",EDGE,"E70.MirrorCS");Q3=makeQuery(id+"F5.imprint","IMPRINT",FACE,{"disambiguationData":[TD([[makeQuery(id+"F5.imprint","IMPRINT",EDGE,{"derivedFrom":subQ3}),-1.0]])]});}
            var Q4;
            {var subQ0=sQuery(id+"F5.wireOp",EDGE,"E47");var subQ1=sQuery(id+"F5.wireOp",EDGE,"E46");var subQ2=makeQuery(id+"F5.imprint","INTERSECT",VERTEX,{"derivedFrom":[subQ1,subQ0]});Q4=makeQuery(id+"F5.imprint","IMPRINT",FACE,{"disambiguationData":[TD([[makeQuery(id+"F5.imprint","IMPRINT",EDGE,{"disambiguationData":[TD([[subQ2,1.0]])],"derivedFrom":subQ1}),-1.0]])]});}
            var Q5;
            {var subQ0=sQuery(id+"F5.wireOp",EDGE,"E51.5.0.0");Q5=makeQuery(id+"F5.imprint","IMPRINT",FACE,{"disambiguationData":[TD([[makeQuery(id+"F5.imprint","IMPRINT",EDGE,{"derivedFrom":subQ0}),1.0]])]});}
            var Q6;
            {var subQ0=sQuery(id+"F5.wireOp",EDGE,"E51.3.0.0");Q6=makeQuery(id+"F5.imprint","IMPRINT",FACE,{"disambiguationData":[TD([[makeQuery(id+"F5.imprint","IMPRINT",EDGE,{"derivedFrom":subQ0}),1.0]])]});}
            var Q7;
            {var subQ0=sQuery(id+"F5.wireOp",EDGE,"E51.1.0.0");Q7=makeQuery(id+"F5.imprint","IMPRINT",FACE,{"disambiguationData":[TD([[makeQuery(id+"F5.imprint","IMPRINT",EDGE,{"derivedFrom":subQ0}),1.0]])]});}
            var Q8;
            {var subQ0=sQuery(id+"F5.wireOp",EDGE,"E50");Q8=makeQuery(id+"F5.imprint","IMPRINT",FACE,{"disambiguationData":[TD([[makeQuery(id+"F5.imprint","IMPRINT",EDGE,{"derivedFrom":subQ0}),-1.0]])]});}
            var Q9;
            {var subQ0=sQuery(id+"F5.wireOp",EDGE,"E61");Q9=makeQuery(id+"F5.imprint","IMPRINT",FACE,{"disambiguationData":[TD([[makeQuery(id+"F5.imprint","IMPRINT",EDGE,{"derivedFrom":subQ0}),-1.0]])]});}
            var Q10;
            {var subQ0=sQuery(id+"F5.wireOp",EDGE,"E62.0.2.0");Q10=makeQuery(id+"F5.imprint","IMPRINT",FACE,{"disambiguationData":[TD([[makeQuery(id+"F5.imprint","IMPRINT",EDGE,{"derivedFrom":subQ0}),-1.0]])]});}
            var Q11;
            {var subQ0=sQuery(id+"F5.wireOp",EDGE,"E62.0.4.0");Q11=makeQuery(id+"F5.imprint","IMPRINT",FACE,{"disambiguationData":[TD([[makeQuery(id+"F5.imprint","IMPRINT",EDGE,{"derivedFrom":subQ0}),-1.0]])]});}
            var Q12;
            {var subQ3=sQuery(id+"F5.wireOp",EDGE,"E62.0.6.0");Q12=makeQuery(id+"F5.imprint","IMPRINT",FACE,{"disambiguationData":[TD([[makeQuery(id+"F5.imprint","IMPRINT",EDGE,{"derivedFrom":subQ3}),-1.0]])]});}
            var Q13;
            {var subQ0=sQuery(id+"F5.wireOp",EDGE,"E45");var subQ1=sQuery(id+"F5.wireOp",EDGE,"E44.0");var subQ2=makeQuery(id+"F5.imprint","INTERSECT",VERTEX,{"derivedFrom":[subQ1,subQ0]});Q13=makeQuery(id+"F5.imprint","IMPRINT",FACE,{"disambiguationData":[TD([[makeQuery(id+"F5.imprint","IMPRINT",EDGE,{"disambiguationData":[TD([[subQ2,-1.0]])],"derivedFrom":subQ1}),1.0]])]});}
            var Q14;
            {var subQ0=sQuery(id+"F5.wireOp",EDGE,"E53.MirrorCS");Q14=makeQuery(id+"F5.imprint","IMPRINT",FACE,{"disambiguationData":[TD([[makeQuery(id+"F5.imprint","IMPRINT",EDGE,{"derivedFrom":subQ0}),-1.0]])]});}
            var Q15;
            {var subQ0=sQuery(id+"F5.wireOp",EDGE,"E55.MirrorCS");Q15=makeQuery(id+"F5.imprint","IMPRINT",FACE,{"disambiguationData":[TD([[makeQuery(id+"F5.imprint","IMPRINT",EDGE,{"derivedFrom":subQ0}),-1.0]])]});}
            var Q16;
            {var subQ0=sQuery(id+"F5.wireOp",EDGE,"E57.MirrorCS");Q16=makeQuery(id+"F5.imprint","IMPRINT",FACE,{"disambiguationData":[TD([[makeQuery(id+"F5.imprint","IMPRINT",EDGE,{"derivedFrom":subQ0}),-1.0]])]});}
            var Q17;
            {var subQ0=sQuery(id+"F5.wireOp",EDGE,"E59.MirrorCS");Q17=makeQuery(id+"F5.imprint","IMPRINT",FACE,{"disambiguationData":[TD([[makeQuery(id+"F5.imprint","IMPRINT",EDGE,{"derivedFrom":subQ0}),-1.0]])]});}
            var Q18;
            {var subQ0=sQuery(id+"F5.wireOp",EDGE,"E53.MirrorCS");Q18=makeQuery(id+"F5.imprint","IMPRINT",FACE,{"disambiguationData":[TD([[makeQuery(id+"F5.imprint","IMPRINT",EDGE,{"derivedFrom":subQ0}),1.0]])]});}
            var Q19;
            {var subQ3=sQuery(id+"F5.wireOp",EDGE,"E79.MirrorCS");Q19=makeQuery(id+"F5.imprint","IMPRINT",FACE,{"disambiguationData":[TD([[makeQuery(id+"F5.imprint","IMPRINT",EDGE,{"derivedFrom":subQ3}),1.0]])]});}
            extrude(context, id + "F32", {"entities" : qUnion([Q0, Q1, Q2, Q3, Q4, Q5, Q6, Q7, Q8, Q9, Q10, Q11, Q12, Q13, Q14, Q15, Q16, Q17, Q18, Q19]), "operationType" : NewBodyOperationType.REMOVE, "oppositeDirection" : true, "depth" : (getVariable(context, 'WT')) * mm});
        }
        {
            var Q0;
            {var subQ3=sQuery(id+"F7.wireOp",EDGE,"E85");Q0=makeQuery(id+"F7.imprint","IMPRINT",FACE,{"disambiguationData":[TD([[makeQuery(id+"F7.imprint","IMPRINT",EDGE,{"derivedFrom":subQ3}),1.0]])]});}
            var Q1;
            {var subQ0=sQuery(id+"F7.wireOp",EDGE,"E89.MirrorCS");Q1=makeQuery(id+"F7.imprint","IMPRINT",FACE,{"disambiguationData":[TD([[makeQuery(id+"F7.imprint","IMPRINT",EDGE,{"derivedFrom":subQ0}),1.0]])]});}
            var Q2;
            {var subQ0=sQuery(id+"F7.wireOp",EDGE,"E86.0.1.0");Q2=makeQuery(id+"F7.imprint","IMPRINT",FACE,{"disambiguationData":[TD([[makeQuery(id+"F7.imprint","IMPRINT",EDGE,{"derivedFrom":subQ0}),-1.0]])]});}
            var Q3;
            {var subQ0=sQuery(id+"F7.wireOp",EDGE,"E91.MirrorCS");Q3=makeQuery(id+"F7.imprint","IMPRINT",FACE,{"disambiguationData":[TD([[makeQuery(id+"F7.imprint","IMPRINT",EDGE,{"derivedFrom":subQ0}),1.0]])]});}
            var Q4;
            {var subQ0=sQuery(id+"F7.wireOp",EDGE,"E86.0.3.0");Q4=makeQuery(id+"F7.imprint","IMPRINT",FACE,{"disambiguationData":[TD([[makeQuery(id+"F7.imprint","IMPRINT",EDGE,{"derivedFrom":subQ0}),-1.0]])]});}
            var Q5;
            {var subQ0=sQuery(id+"F7.wireOp",EDGE,"E93.MirrorCS");Q5=makeQuery(id+"F7.imprint","IMPRINT",FACE,{"disambiguationData":[TD([[makeQuery(id+"F7.imprint","IMPRINT",EDGE,{"derivedFrom":subQ0}),1.0]])]});}
            var Q6;
            {var subQ0=sQuery(id+"F7.wireOp",EDGE,"E86.0.5.0");Q6=makeQuery(id+"F7.imprint","IMPRINT",FACE,{"disambiguationData":[TD([[makeQuery(id+"F7.imprint","IMPRINT",EDGE,{"derivedFrom":subQ0}),-1.0]])]});}
            var Q7;
            {var subQ3=sQuery(id+"F7.wireOp",EDGE,"E95.MirrorCS");Q7=makeQuery(id+"F7.imprint","IMPRINT",FACE,{"disambiguationData":[TD([[makeQuery(id+"F7.imprint","IMPRINT",EDGE,{"derivedFrom":subQ3}),1.0]])]});}
            extrude(context, id + "F33", {"entities" : qUnion([Q0, Q1, Q2, Q3, Q4, Q5, Q6, Q7]), "operationType" : NewBodyOperationType.REMOVE, "oppositeDirection" : true, "depth" : (getVariable(context, 'WT')) * mm});
        }
        {
            var Q0;
            {var subQ4=sQuery(id+"F13.wireOp",EDGE,"E124.0");Q0=makeQuery(id+"F13.imprint","IMPRINT",FACE,{"disambiguationData":[TD([[makeQuery(id+"F13.imprint","IMPRINT",EDGE,{"derivedFrom":subQ4}),-1.0]])]});}
            extrude(context, id + "F34", {"entities" : qUnion([Q0]), "operationType" : NewBodyOperationType.REMOVE, "depth" : (getVariable(context, 'WT')) * mm});
        }
        {
            var Q0;
            {var subQ9=sQuery(id+"F15.wireOp",EDGE,"E156.0");Q0=makeQuery(id+"F15.imprint","IMPRINT",FACE,{"disambiguationData":[TD([[makeQuery(id+"F15.imprint","IMPRINT",EDGE,{"derivedFrom":subQ9}),1.0]])]});}
            extrude(context, id + "F35", {"entities" : qUnion([Q0]), "operationType" : NewBodyOperationType.REMOVE, "depth" : (getVariable(context, 'WT')) * mm});
        }
        {
            var Q0;
            {var subQ3=sQuery(id+"F9.wireOp",EDGE,"E101.7");Q0=makeQuery(id+"F9.imprint","IMPRINT",FACE,{"disambiguationData":[TD([[makeQuery(id+"F9.imprint","IMPRINT",EDGE,{"derivedFrom":subQ3}),-1.0]])]});}
            var Q1;
            {var subQ0=sQuery(id+"F9.wireOp",EDGE,"E101.33");Q1=makeQuery(id+"F9.imprint","IMPRINT",FACE,{"disambiguationData":[TD([[makeQuery(id+"F9.imprint","IMPRINT",EDGE,{"derivedFrom":subQ0}),1.0]])]});}
            var Q2;
            {var subQ0=sQuery(id+"F9.wireOp",EDGE,"E101.8");Q2=makeQuery(id+"F9.imprint","IMPRINT",FACE,{"disambiguationData":[TD([[makeQuery(id+"F9.imprint","IMPRINT",EDGE,{"derivedFrom":subQ0}),1.0]])]});}
            var Q3;
            {var subQ0=sQuery(id+"F9.wireOp",EDGE,"E101.10");Q3=makeQuery(id+"F9.imprint","IMPRINT",FACE,{"disambiguationData":[TD([[makeQuery(id+"F9.imprint","IMPRINT",EDGE,{"derivedFrom":subQ0}),1.0]])]});}
            var Q4;
            {var subQ0=sQuery(id+"F9.wireOp",EDGE,"E101.12");Q4=makeQuery(id+"F9.imprint","IMPRINT",FACE,{"disambiguationData":[TD([[makeQuery(id+"F9.imprint","IMPRINT",EDGE,{"derivedFrom":subQ0}),1.0]])]});}
            var Q5;
            {var subQ0=sQuery(id+"F9.wireOp",EDGE,"E101.3");var subQ1=sQuery(id+"F9.wireOp",EDGE,"E101.1");var subQ2=makeQuery(id+"F9.imprint","INTERSECT",VERTEX,{"derivedFrom":[subQ1,subQ0]});Q5=makeQuery(id+"F9.imprint","IMPRINT",FACE,{"disambiguationData":[TD([[makeQuery(id+"F9.imprint","IMPRINT",EDGE,{"disambiguationData":[TD([[subQ2,-1.0]])],"derivedFrom":subQ1}),-1.0]])]});}
            var Q6;
            {var subQ3=sQuery(id+"F9.wireOp",EDGE,"E101.14");Q6=makeQuery(id+"F9.imprint","IMPRINT",FACE,{"disambiguationData":[TD([[makeQuery(id+"F9.imprint","IMPRINT",EDGE,{"derivedFrom":subQ3}),-1.0]])]});}
            var Q7;
            {var subQ0=sQuery(id+"F9.wireOp",EDGE,"E101.15");Q7=makeQuery(id+"F9.imprint","IMPRINT",FACE,{"disambiguationData":[TD([[makeQuery(id+"F9.imprint","IMPRINT",EDGE,{"derivedFrom":subQ0}),1.0]])]});}
            var Q8;
            {var subQ0=sQuery(id+"F9.wireOp",EDGE,"E101.17");Q8=makeQuery(id+"F9.imprint","IMPRINT",FACE,{"disambiguationData":[TD([[makeQuery(id+"F9.imprint","IMPRINT",EDGE,{"derivedFrom":subQ0}),-1.0]])]});}
            var Q9;
            {var subQ0=sQuery(id+"F9.wireOp",EDGE,"E101.18");Q9=makeQuery(id+"F9.imprint","IMPRINT",FACE,{"disambiguationData":[TD([[makeQuery(id+"F9.imprint","IMPRINT",EDGE,{"derivedFrom":subQ0}),1.0]])]});}
            var Q10;
            {var subQ3=sQuery(id+"F9.wireOp",EDGE,"E101.21");Q10=makeQuery(id+"F9.imprint","IMPRINT",FACE,{"disambiguationData":[TD([[makeQuery(id+"F9.imprint","IMPRINT",EDGE,{"derivedFrom":subQ3}),-1.0]])]});}
            var Q11;
            {var subQ0=sQuery(id+"F9.wireOp",EDGE,"E101.22");Q11=makeQuery(id+"F9.imprint","IMPRINT",FACE,{"disambiguationData":[TD([[makeQuery(id+"F9.imprint","IMPRINT",EDGE,{"derivedFrom":subQ0}),1.0]])]});}
            var Q12;
            {var subQ0=sQuery(id+"F9.wireOp",EDGE,"E101.24");Q12=makeQuery(id+"F9.imprint","IMPRINT",FACE,{"disambiguationData":[TD([[makeQuery(id+"F9.imprint","IMPRINT",EDGE,{"derivedFrom":subQ0}),1.0]])]});}
            var Q13;
            {var subQ0=sQuery(id+"F9.wireOp",EDGE,"E101.26");Q13=makeQuery(id+"F9.imprint","IMPRINT",FACE,{"disambiguationData":[TD([[makeQuery(id+"F9.imprint","IMPRINT",EDGE,{"derivedFrom":subQ0}),1.0]])]});}
            var Q14;
            {var subQ0=sQuery(id+"F9.wireOp",EDGE,"E101.2");var subQ1=sQuery(id+"F9.wireOp",EDGE,"E101.0");var subQ2=makeQuery(id+"F9.imprint","INTERSECT",VERTEX,{"derivedFrom":[subQ1,subQ0]});Q14=makeQuery(id+"F9.imprint","IMPRINT",FACE,{"disambiguationData":[TD([[makeQuery(id+"F9.imprint","IMPRINT",EDGE,{"disambiguationData":[TD([[subQ2,-1.0]])],"derivedFrom":subQ1}),1.0]])]});}
            var Q15;
            {var subQ3=sQuery(id+"F9.wireOp",EDGE,"E101.28");Q15=makeQuery(id+"F9.imprint","IMPRINT",FACE,{"disambiguationData":[TD([[makeQuery(id+"F9.imprint","IMPRINT",EDGE,{"derivedFrom":subQ3}),-1.0]])]});}
            var Q16;
            {var subQ0=sQuery(id+"F9.wireOp",EDGE,"E101.29");Q16=makeQuery(id+"F9.imprint","IMPRINT",FACE,{"disambiguationData":[TD([[makeQuery(id+"F9.imprint","IMPRINT",EDGE,{"derivedFrom":subQ0}),1.0]])]});}
            var Q17;
            {var subQ0=sQuery(id+"F9.wireOp",EDGE,"E101.31");Q17=makeQuery(id+"F9.imprint","IMPRINT",FACE,{"disambiguationData":[TD([[makeQuery(id+"F9.imprint","IMPRINT",EDGE,{"derivedFrom":subQ0}),1.0]])]});}
            extrude(context, id + "F36", {"entities" : qUnion([Q0, Q1, Q2, Q3, Q4, Q5, Q6, Q7, Q8, Q9, Q10, Q11, Q12, Q13, Q14, Q15, Q16, Q17]), "operationType" : NewBodyOperationType.REMOVE, "depth" : (getVariable(context, 'WT')) * mm});
        }
        {
            var Q0;
            {var subQ8=sQuery(id+"F17.wireOp",EDGE,"E193");Q0=makeQuery(id+"F17.imprint","IMPRINT",FACE,{"disambiguationData":[TD([[makeQuery(id+"F17.imprint","IMPRINT",EDGE,{"derivedFrom":subQ8}),1.0]])]});}
            extrude(context, id + "F37", {"entities" : qUnion([Q0]), "depth" : (getVariable(context, 'WT')) * mm});
        }
        {
            var Q0;
            {var subQ14=sQuery(id+"F17.wireOp",EDGE,"E193");Q0=makeQuery(id+"F17.imprint","IMPRINT",FACE,{"disambiguationData":[TD([[makeQuery(id+"F17.imprint","IMPRINT",EDGE,{"derivedFrom":subQ14}),1.0]])]});}
            extrude(context, id + "F38", {"entities" : qUnion([Q0]), "operationType" : NewBodyOperationType.REMOVE, "depth" : (getVariable(context, 'WT')) * mm});
        }
        {
            var Q0;
            {var subQ8=sQuery(id+"F19.wireOp",EDGE,"E229");Q0=makeQuery(id+"F19.imprint","IMPRINT",FACE,{"disambiguationData":[TD([[makeQuery(id+"F19.imprint","IMPRINT",EDGE,{"derivedFrom":subQ8}),1.0]])]});}
            extrude(context, id + "F39", {"entities" : qUnion([Q0]), "depth" : (getVariable(context, 'WT')) * mm});
        }
        {
            var Q0;
            {var subQ8=sQuery(id+"F19.wireOp",EDGE,"E229");Q0=makeQuery(id+"F19.imprint","IMPRINT",FACE,{"disambiguationData":[TD([[makeQuery(id+"F19.imprint","IMPRINT",EDGE,{"derivedFrom":subQ8}),1.0]])]});}
            extrude(context, id + "F40", {"entities" : qUnion([Q0]), "operationType" : NewBodyOperationType.REMOVE, "depth" : (getVariable(context, 'WT')) * mm});
        }
        {
            var Q0;
            Q0=makeQuery(id+"F22.imprint","IMPRINT",FACE,{"disambiguationData":[TD([[makeQuery(id+"F22.imprint","IMPRINT",EDGE,{"derivedFrom":sQuery(id+"F22.wireOp",EDGE,"E265.0")}),-1.0]])]});
            var Q1;
            Q1=makeQuery(id+"F22.imprint","IMPRINT",FACE,{"disambiguationData":[TD([[makeQuery(id+"F22.imprint","IMPRINT",EDGE,{"derivedFrom":sQuery(id+"F22.wireOp",EDGE,"E265.1")}),-1.0]])]});
            var Q2;
            Q2=makeQuery(id+"F22.imprint","IMPRINT",FACE,{"disambiguationData":[TD([[makeQuery(id+"F22.imprint","IMPRINT",EDGE,{"derivedFrom":sQuery(id+"F22.wireOp",EDGE,"E266.0.1.6")}),-1.0]])]});
            var Q3;
            Q3=makeQuery(id+"F22.imprint","IMPRINT",FACE,{"disambiguationData":[TD([[makeQuery(id+"F22.imprint","IMPRINT",EDGE,{"derivedFrom":sQuery(id+"F22.wireOp",EDGE,"E266.0.2.6")}),-1.0]])]});
            var Q4;
            Q4=makeQuery(id+"F22.imprint","IMPRINT",FACE,{"disambiguationData":[TD([[makeQuery(id+"F22.imprint","IMPRINT",EDGE,{"derivedFrom":sQuery(id+"F22.wireOp",EDGE,"E266.0.3.6")}),-1.0]])]});
            var Q5;
            Q5=makeQuery(id+"F22.imprint","IMPRINT",FACE,{"disambiguationData":[TD([[makeQuery(id+"F22.imprint","IMPRINT",EDGE,{"derivedFrom":sQuery(id+"F22.wireOp",EDGE,"E266.0.4.6")}),-1.0]])]});
            extrude(context, id + "F41", {"entities" : qUnion([Q0, Q1, Q2, Q3, Q4, Q5]), "oppositeDirection" : true, "depth" : (getVariable(context, 'WT')) * mm});
        }
        {
            var Q0;
            Q0=makeQuery(id+"F24.imprint","IMPRINT",FACE,{"disambiguationData":[TD([[makeQuery(id+"F24.imprint","IMPRINT",EDGE,{"derivedFrom":sQuery(id+"F24.wireOp",EDGE,"E299.0")}),-1.0]])]});
            extrude(context, id + "F42", {"entities" : qUnion([Q0]), "oppositeDirection" : true, "depth" : (getVariable(context, 'WT')) * mm});
        }
        {
            var Q0;
            Q0=makeQuery(id+"F3.imprint","IMPRINT",FACE,{"disambiguationData":[TD([[makeQuery(id+"F3.imprint","IMPRINT",EDGE,{"derivedFrom":sQuery(id+"F3.wireOp",EDGE,"E37.5")}),1.0]])]});
            extrude(context, id + "F43", {"entities" : qUnion([Q0]), "oppositeDirection" : true, "depth" : (getVariable(context, 'WT')) * mm});
        }
        {
            var Q0;
            {var subQ3=sQuery(id+"F23.wireOp",EDGE,"E282.6");Q0=makeQuery(id+"F23.imprint","IMPRINT",FACE,{"disambiguationData":[TD([[makeQuery(id+"F23.imprint","IMPRINT",EDGE,{"derivedFrom":subQ3}),-1.0]])]});}
            var Q1;
            {var subQ0=sQuery(id+"F23.wireOp",EDGE,"E283.0");Q1=makeQuery(id+"F23.imprint","IMPRINT",FACE,{"disambiguationData":[TD([[makeQuery(id+"F23.imprint","IMPRINT",EDGE,{"derivedFrom":subQ0}),-1.0]])]});}
            var Q2;
            {var subQ0=sQuery(id+"F23.wireOp",EDGE,"E283.2");Q2=makeQuery(id+"F23.imprint","IMPRINT",FACE,{"disambiguationData":[TD([[makeQuery(id+"F23.imprint","IMPRINT",EDGE,{"derivedFrom":subQ0}),-1.0]])]});}
            var Q3;
            {var subQ0=sQuery(id+"F23.wireOp",EDGE,"E283.4");Q3=makeQuery(id+"F23.imprint","IMPRINT",FACE,{"disambiguationData":[TD([[makeQuery(id+"F23.imprint","IMPRINT",EDGE,{"derivedFrom":subQ0}),-1.0]])]});}
            var Q4;
            {var subQ0=sQuery(id+"F23.wireOp",EDGE,"E283.6");Q4=makeQuery(id+"F23.imprint","IMPRINT",FACE,{"disambiguationData":[TD([[makeQuery(id+"F23.imprint","IMPRINT",EDGE,{"derivedFrom":subQ0}),-1.0]])]});}
            var Q5;
            {var subQ0=sQuery(id+"F23.wireOp",EDGE,"E267.2");var subQ1=sQuery(id+"F23.wireOp",EDGE,"E267.1");var subQ2=makeQuery(id+"F23.imprint","INTERSECT",VERTEX,{"derivedFrom":[subQ1,subQ0]});Q5=makeQuery(id+"F23.imprint","IMPRINT",FACE,{"disambiguationData":[TD([[makeQuery(id+"F23.imprint","IMPRINT",EDGE,{"disambiguationData":[TD([[subQ2,-1.0]])],"derivedFrom":subQ1}),-1.0]])]});}
            var Q6;
            {var subQ3=sQuery(id+"F23.wireOp",EDGE,"E284.0");Q6=makeQuery(id+"F23.imprint","IMPRINT",FACE,{"disambiguationData":[TD([[makeQuery(id+"F23.imprint","IMPRINT",EDGE,{"derivedFrom":subQ3}),1.0]])]});}
            var Q7;
            {var subQ0=sQuery(id+"F23.wireOp",EDGE,"E285.0");Q7=makeQuery(id+"F23.imprint","IMPRINT",FACE,{"disambiguationData":[TD([[makeQuery(id+"F23.imprint","IMPRINT",EDGE,{"derivedFrom":subQ0}),-1.0]])]});}
            var Q8;
            {var subQ3=sQuery(id+"F23.wireOp",EDGE,"E285.2");Q8=makeQuery(id+"F23.imprint","IMPRINT",FACE,{"disambiguationData":[TD([[makeQuery(id+"F23.imprint","IMPRINT",EDGE,{"derivedFrom":subQ3}),-1.0]])]});}
            var Q9;
            {var subQ0=sQuery(id+"F23.wireOp",EDGE,"E285.4");Q9=makeQuery(id+"F23.imprint","IMPRINT",FACE,{"disambiguationData":[TD([[makeQuery(id+"F23.imprint","IMPRINT",EDGE,{"derivedFrom":subQ0}),-1.0]])]});}
            var Q10;
            {var subQ0=sQuery(id+"F23.wireOp",EDGE,"E270");var subQ1=sQuery(id+"F23.wireOp",EDGE,"E269");var subQ2=makeQuery(id+"F23.imprint","INTERSECT",VERTEX,{"derivedFrom":[subQ1,subQ0]});Q10=makeQuery(id+"F23.imprint","IMPRINT",FACE,{"disambiguationData":[TD([[makeQuery(id+"F23.imprint","IMPRINT",EDGE,{"disambiguationData":[TD([[subQ2,1.0]])],"derivedFrom":subQ1}),-1.0]])]});}
            var Q11;
            {var subQ3=sQuery(id+"F23.wireOp",EDGE,"E298");Q11=makeQuery(id+"F23.imprint","IMPRINT",FACE,{"disambiguationData":[TD([[makeQuery(id+"F23.imprint","IMPRINT",EDGE,{"derivedFrom":subQ3}),-1.0]])]});}
            var Q12;
            {var subQ0=sQuery(id+"F23.wireOp",EDGE,"E294");Q12=makeQuery(id+"F23.imprint","IMPRINT",FACE,{"disambiguationData":[TD([[makeQuery(id+"F23.imprint","IMPRINT",EDGE,{"derivedFrom":subQ0}),-1.0]])]});}
            var Q13;
            {var subQ0=sQuery(id+"F23.wireOp",EDGE,"E293");Q13=makeQuery(id+"F23.imprint","IMPRINT",FACE,{"disambiguationData":[TD([[makeQuery(id+"F23.imprint","IMPRINT",EDGE,{"derivedFrom":subQ0}),-1.0]])]});}
            var Q14;
            {var subQ0=sQuery(id+"F23.wireOp",EDGE,"E291");Q14=makeQuery(id+"F23.imprint","IMPRINT",FACE,{"disambiguationData":[TD([[makeQuery(id+"F23.imprint","IMPRINT",EDGE,{"derivedFrom":subQ0}),-1.0]])]});}
            var Q15;
            {var subQ3=sQuery(id+"F23.wireOp",EDGE,"E290");Q15=makeQuery(id+"F23.imprint","IMPRINT",FACE,{"disambiguationData":[TD([[makeQuery(id+"F23.imprint","IMPRINT",EDGE,{"derivedFrom":subQ3}),1.0]])]});}
            var Q16;
            {var subQ0=sQuery(id+"F23.wireOp",EDGE,"E269");var subQ1=sQuery(id+"F23.wireOp",EDGE,"E268");var subQ2=makeQuery(id+"F23.imprint","INTERSECT",VERTEX,{"derivedFrom":[subQ1,subQ0]});Q16=makeQuery(id+"F23.imprint","IMPRINT",FACE,{"disambiguationData":[TD([[makeQuery(id+"F23.imprint","IMPRINT",EDGE,{"disambiguationData":[TD([[subQ2,1.0]])],"derivedFrom":subQ1}),-1.0]])]});}
            var Q17;
            {var subQ0=sQuery(id+"F23.wireOp",EDGE,"E282.0");Q17=makeQuery(id+"F23.imprint","IMPRINT",FACE,{"disambiguationData":[TD([[makeQuery(id+"F23.imprint","IMPRINT",EDGE,{"derivedFrom":subQ0}),-1.0]])]});}
            var Q18;
            {var subQ4=sQuery(id+"F23.wireOp",EDGE,"E282.2");Q18=makeQuery(id+"F23.imprint","IMPRINT",FACE,{"disambiguationData":[TD([[makeQuery(id+"F23.imprint","IMPRINT",EDGE,{"derivedFrom":subQ4}),-1.0]])]});}
            var Q19;
            {var subQ0=sQuery(id+"F23.wireOp",EDGE,"E282.4");Q19=makeQuery(id+"F23.imprint","IMPRINT",FACE,{"disambiguationData":[TD([[makeQuery(id+"F23.imprint","IMPRINT",EDGE,{"derivedFrom":subQ0}),-1.0]])]});}
            extrude(context, id + "F44", {"entities" : qUnion([Q0, Q1, Q2, Q3, Q4, Q5, Q6, Q7, Q8, Q9, Q10, Q11, Q12, Q13, Q14, Q15, Q16, Q17, Q18, Q19]), "operationType" : NewBodyOperationType.REMOVE, "oppositeDirection" : true, "depth" : (getVariable(context, 'WT')) * mm});
        }
        {
            var Q0;
            {var subQ0=sQuery(id+"F23.wireOp",EDGE,"E284.0");Q0=makeQuery(id+"F23.imprint","IMPRINT",FACE,{"disambiguationData":[TD([[makeQuery(id+"F23.imprint","IMPRINT",EDGE,{"derivedFrom":subQ0}),-1.0]])]});}
            var Q1;
            {var subQ0=sQuery(id+"F23.wireOp",EDGE,"E285.1");Q1=makeQuery(id+"F23.imprint","IMPRINT",FACE,{"disambiguationData":[TD([[makeQuery(id+"F23.imprint","IMPRINT",EDGE,{"derivedFrom":subQ0}),-1.0]])]});}
            var Q2;
            {var subQ0=sQuery(id+"F23.wireOp",EDGE,"E285.3");Q2=makeQuery(id+"F23.imprint","IMPRINT",FACE,{"disambiguationData":[TD([[makeQuery(id+"F23.imprint","IMPRINT",EDGE,{"derivedFrom":subQ0}),-1.0]])]});}
            var Q3;
            {var subQ0=sQuery(id+"F23.wireOp",EDGE,"E285.5");Q3=makeQuery(id+"F23.imprint","IMPRINT",FACE,{"disambiguationData":[TD([[makeQuery(id+"F23.imprint","IMPRINT",EDGE,{"derivedFrom":subQ0}),-1.0]])]});}
            var Q4;
            {var subQ0=sQuery(id+"F23.wireOp",EDGE,"E295");Q4=makeQuery(id+"F23.imprint","IMPRINT",FACE,{"disambiguationData":[TD([[makeQuery(id+"F23.imprint","IMPRINT",EDGE,{"derivedFrom":subQ0}),-1.0]])]});}
            var Q5;
            {var subQ0=sQuery(id+"F23.wireOp",EDGE,"E294");Q5=makeQuery(id+"F23.imprint","IMPRINT",FACE,{"disambiguationData":[TD([[makeQuery(id+"F23.imprint","IMPRINT",EDGE,{"derivedFrom":subQ0}),1.0]])]});}
            var Q6;
            {var subQ0=sQuery(id+"F23.wireOp",EDGE,"E292");Q6=makeQuery(id+"F23.imprint","IMPRINT",FACE,{"disambiguationData":[TD([[makeQuery(id+"F23.imprint","IMPRINT",EDGE,{"derivedFrom":subQ0}),-1.0]])]});}
            var Q7;
            {var subQ0=sQuery(id+"F23.wireOp",EDGE,"E290");Q7=makeQuery(id+"F23.imprint","IMPRINT",FACE,{"disambiguationData":[TD([[makeQuery(id+"F23.imprint","IMPRINT",EDGE,{"derivedFrom":subQ0}),-1.0]])]});}
            var Q8;
            {var subQ0=sQuery(id+"F23.wireOp",EDGE,"E282.0");Q8=makeQuery(id+"F23.imprint","IMPRINT",FACE,{"disambiguationData":[TD([[makeQuery(id+"F23.imprint","IMPRINT",EDGE,{"derivedFrom":subQ0}),1.0]])]});}
            var Q9;
            {var subQ0=sQuery(id+"F23.wireOp",EDGE,"E282.1");Q9=makeQuery(id+"F23.imprint","IMPRINT",FACE,{"disambiguationData":[TD([[makeQuery(id+"F23.imprint","IMPRINT",EDGE,{"derivedFrom":subQ0}),-1.0]])]});}
            var Q10;
            {var subQ0=sQuery(id+"F23.wireOp",EDGE,"E282.3");Q10=makeQuery(id+"F23.imprint","IMPRINT",FACE,{"disambiguationData":[TD([[makeQuery(id+"F23.imprint","IMPRINT",EDGE,{"derivedFrom":subQ0}),-1.0]])]});}
            var Q11;
            {var subQ0=sQuery(id+"F23.wireOp",EDGE,"E282.5");Q11=makeQuery(id+"F23.imprint","IMPRINT",FACE,{"disambiguationData":[TD([[makeQuery(id+"F23.imprint","IMPRINT",EDGE,{"derivedFrom":subQ0}),-1.0]])]});}
            var Q12;
            {var subQ3=sQuery(id+"F23.wireOp",EDGE,"E283.0");Q12=makeQuery(id+"F23.imprint","IMPRINT",FACE,{"disambiguationData":[TD([[makeQuery(id+"F23.imprint","IMPRINT",EDGE,{"derivedFrom":subQ3}),1.0]])]});}
            var Q13;
            {var subQ0=sQuery(id+"F23.wireOp",EDGE,"E283.1");Q13=makeQuery(id+"F23.imprint","IMPRINT",FACE,{"disambiguationData":[TD([[makeQuery(id+"F23.imprint","IMPRINT",EDGE,{"derivedFrom":subQ0}),-1.0]])]});}
            var Q14;
            {var subQ0=sQuery(id+"F23.wireOp",EDGE,"E283.3");Q14=makeQuery(id+"F23.imprint","IMPRINT",FACE,{"disambiguationData":[TD([[makeQuery(id+"F23.imprint","IMPRINT",EDGE,{"derivedFrom":subQ0}),-1.0]])]});}
            var Q15;
            {var subQ0=sQuery(id+"F23.wireOp",EDGE,"E283.5");Q15=makeQuery(id+"F23.imprint","IMPRINT",FACE,{"disambiguationData":[TD([[makeQuery(id+"F23.imprint","IMPRINT",EDGE,{"derivedFrom":subQ0}),-1.0]])]});}
            var Q16;
            {var subQ3=sQuery(id+"F23.wireOp",EDGE,"E297.0");Q16=makeQuery(id+"F23.imprint","IMPRINT",FACE,{"disambiguationData":[TD([[makeQuery(id+"F23.imprint","IMPRINT",EDGE,{"derivedFrom":subQ3}),-1.0]])]});}
            extrude(context, id + "F45", {"entities" : qUnion([Q0, Q1, Q2, Q3, Q4, Q5, Q6, Q7, Q8, Q9, Q10, Q11, Q12, Q13, Q14, Q15, Q16]), "operationType" : NewBodyOperationType.REMOVE, "oppositeDirection" : true, "depth" : (getVariable(context, 'WT')) * mm});
        }
    });
